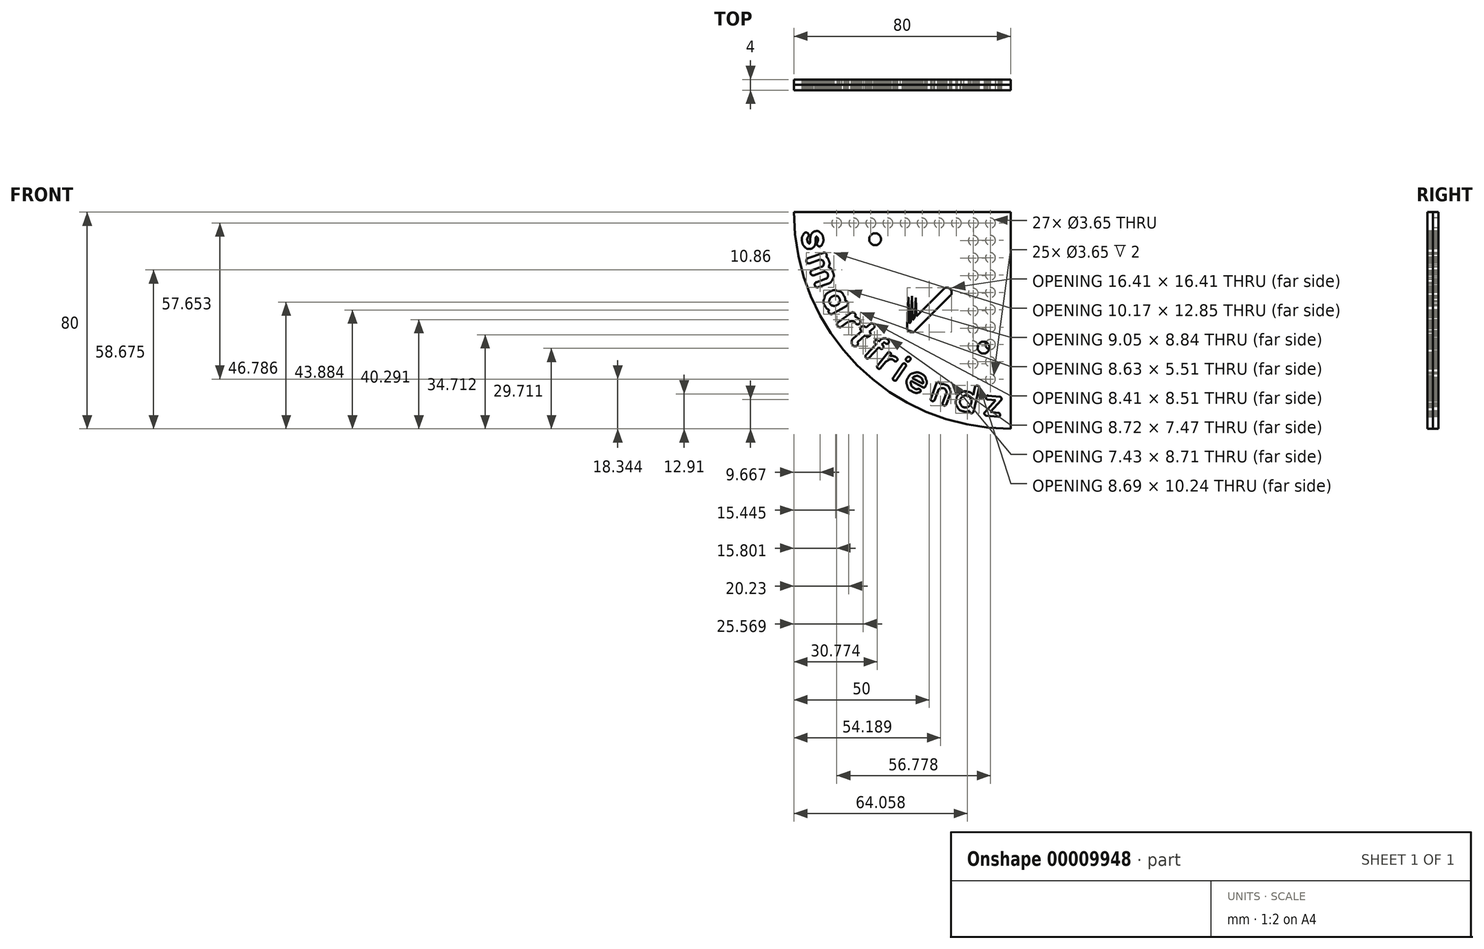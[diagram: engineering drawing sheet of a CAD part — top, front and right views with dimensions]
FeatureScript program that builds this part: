
annotation { "Feature Type Name" : "Feature", "Feature Type Description" : "" }
export const myFeature = defineFeature(function(context is Context, id is Id, definition is map)
    precondition{}
    {
        {
            var Q0;
            Q0=qCreatedBy(makeId("Front.planeOp"),FACE);
            var sketch = newSketch(context, id + "F0", { "sketchPlane" : qUnion([Q0])});
            skFitSpline(sketch, "E0", {"points": [v(17.73, 12.09) * mm, v(17.4, 12.41) * mm, v(16.98, 12.59) * mm, v(16.53, 12.59) * mm]});
            skFitSpline(sketch, "E1", {"points": [v(16.53, 12.59) * mm, v(16.05, 12.59) * mm, v(15.65, 12.41) * mm, v(15.33, 12.09) * mm]});
            skLineSegment(sketch, "E2", {"start": v(15.33, 12.09) * mm, "end": v(5.27, 2.03) * mm});
            skLineSegment(sketch, "E3", {"start": v(5.27, 2.03) * mm, "end": v(5.07, 8.86) * mm});
            skFitSpline(sketch, "E4", {"points": [v(5.07, 8.86) * mm, v(5.04, 8.88) * mm, v(5.02, 8.9) * mm, v(5, 8.93) * mm]});
            skLineSegment(sketch, "E5", {"start": v(5, 8.93) * mm, "end": v(4.72, 1.5) * mm});
            skLineSegment(sketch, "E6", {"start": v(4.72, 1.5) * mm, "end": v(3.94, 0.73) * mm});
            skLineSegment(sketch, "E7", {"start": v(3.94, 0.73) * mm, "end": v(3.67, 9.53) * mm});
            skLineSegment(sketch, "E8", {"start": v(3.67, 9.53) * mm, "end": v(3.64, 9.53) * mm});
            skLineSegment(sketch, "E9", {"start": v(3.64, 9.53) * mm, "end": v(3.32, 0.1) * mm});
            skLineSegment(sketch, "E10", {"start": v(3.32, 0.1) * mm, "end": v(2.64, -0.57) * mm});
            skLineSegment(sketch, "E11", {"start": v(2.64, -0.57) * mm, "end": v(2.37, 9) * mm});
            skFitSpline(sketch, "E12", {"points": [v(2.37, 9) * mm, v(2.35, 9) * mm, v(2.33, 8.97) * mm, v(2.32, 8.93) * mm]});
            skLineSegment(sketch, "E13", {"start": v(2.32, 8.93) * mm, "end": v(1.94, -1.57) * mm});
            skFitSpline(sketch, "E14", {"points": [v(1.94, -1.57) * mm, v(1.9, -1.72) * mm, v(1.87, -1.9) * mm, v(1.87, -2.07) * mm]});
            skFitSpline(sketch, "E15", {"points": [v(1.87, -2.07) * mm, v(1.87, -2.55) * mm, v(2.04, -2.95) * mm, v(2.37, -3.28) * mm]});
            skFitSpline(sketch, "E16", {"points": [v(2.37, -3.28) * mm, v(2.7, -3.6) * mm, v(3.12, -3.78) * mm, v(3.6, -3.8) * mm]});
            skFitSpline(sketch, "E17", {"points": [v(3.6, -3.8) * mm, v(4.07, -3.8) * mm, v(4.47, -3.65) * mm, v(4.82, -3.3) * mm]});
            skLineSegment(sketch, "E18", {"start": v(4.82, -3.3) * mm, "end": v(17.75, 9.63) * mm});
            skFitSpline(sketch, "E19", {"points": [v(17.75, 9.63) * mm, v(18.08, 9.98) * mm, v(18.25, 10.38) * mm, v(18.25, 10.86) * mm]});
            skFitSpline(sketch, "E20", {"points": [v(18.25, 10.86) * mm, v(18.23, 11.34) * mm, v(18.08, 11.76) * mm, v(17.73, 12.09) * mm]});
            skFitSpline(sketch, "E21", {"points": [v(9.35, 19.77) * mm, v(9.35, 20.24) * mm, v(9.17, 20.64) * mm, v(8.82, 21) * mm]});
            skFitSpline(sketch, "E22", {"points": [v(8.82, 21) * mm, v(8.5, 21.32) * mm, v(8.07, 21.5) * mm, v(7.62, 21.5) * mm]});
            skFitSpline(sketch, "E23", {"points": [v(7.62, 21.5) * mm, v(7.45, 21.5) * mm, v(7.3, 21.47) * mm, v(7.15, 21.42) * mm]});
            skLineSegment(sketch, "E24", {"start": v(7.15, 21.42) * mm, "end": v(-3.41, 21.1) * mm});
            skFitSpline(sketch, "E25", {"points": [v(-3.41, 21.1) * mm, v(-3.44, 21.07) * mm, v(-3.46, 21.07) * mm, v(-3.46, 21.04) * mm]});
            skLineSegment(sketch, "E26", {"start": v(-3.46, 21.04) * mm, "end": v(6.15, 20.7) * mm});
            skLineSegment(sketch, "E27", {"start": v(6.15, 20.7) * mm, "end": v(5.47, 20.02) * mm});
            skLineSegment(sketch, "E28", {"start": v(5.47, 20.02) * mm, "end": v(-4.09, 19.74) * mm});
            skLineSegment(sketch, "E29", {"start": v(-4.09, 19.74) * mm, "end": v(4.84, 19.42) * mm});
            skLineSegment(sketch, "E30", {"start": v(4.84, 19.42) * mm, "end": v(4.07, 18.64) * mm});
            skLineSegment(sketch, "E31", {"start": v(4.07, 18.64) * mm, "end": v(-3.56, 18.42) * mm});
            skFitSpline(sketch, "E32", {"points": [v(-3.56, 18.42) * mm, v(-3.54, 18.4) * mm, v(-3.54, 18.4) * mm, v(-3.51, 18.37) * mm]});
            skLineSegment(sketch, "E33", {"start": v(-3.51, 18.37) * mm, "end": v(3.57, 18.11) * mm});
            skLineSegment(sketch, "E34", {"start": v(3.57, 18.11) * mm, "end": v(-6.54, 8.06) * mm});
            skFitSpline(sketch, "E35", {"points": [v(-6.54, 8.06) * mm, v(-6.86, 7.73) * mm, v(-7.04, 7.3) * mm, v(-7.04, 6.86) * mm]});
            skFitSpline(sketch, "E36", {"points": [v(-7.04, 6.86) * mm, v(-7.04, 6.38) * mm, v(-6.86, 5.98) * mm, v(-6.54, 5.66) * mm]});
            skFitSpline(sketch, "E37", {"points": [v(-6.54, 5.66) * mm, v(-6.21, 5.33) * mm, v(-5.79, 5.16) * mm, v(-5.31, 5.13) * mm]});
            skFitSpline(sketch, "E38", {"points": [v(-5.31, 5.13) * mm, v(-4.84, 5.13) * mm, v(-4.44, 5.28) * mm, v(-4.09, 5.63) * mm]});
            skLineSegment(sketch, "E39", {"start": v(-4.09, 5.63) * mm, "end": v(8.85, 18.57) * mm});
            skFitSpline(sketch, "E40", {"points": [v(8.85, 18.57) * mm, v(9.2, 18.9) * mm, v(9.35, 19.3) * mm, v(9.35, 19.77) * mm]});
            skFitSpline(sketch, "E41", {"points": [v(-33.8, 26.97) * mm, v(-33.43, 27.05) * mm, v(-33.08, 27.22) * mm, v(-32.76, 27.52) * mm]});
            skFitSpline(sketch, "E42", {"points": [v(-32.76, 27.52) * mm, v(-32.43, 27.82) * mm, v(-32.18, 28.22) * mm, v(-32.06, 28.72) * mm]});
            skFitSpline(sketch, "E43", {"points": [v(-32.06, 28.72) * mm, v(-31.93, 29.2) * mm, v(-31.88, 29.7) * mm, v(-31.88, 30.25) * mm]});
            skLineSegment(sketch, "E44", {"start": v(-31.88, 30.25) * mm, "end": v(-31.88, 30.27) * mm});
            skLineSegment(sketch, "E45", {"start": v(-31.88, 30.27) * mm, "end": v(-31.88, 30.32) * mm});
            skFitSpline(sketch, "E46", {"points": [v(-31.88, 30.32) * mm, v(-31.88, 30.82) * mm, v(-31.83, 31.17) * mm, v(-31.73, 31.4) * mm]});
            skFitSpline(sketch, "E47", {"points": [v(-31.73, 31.4) * mm, v(-31.72, 31.45) * mm, v(-31.7, 31.48) * mm, v(-31.68, 31.5) * mm]});
            skFitSpline(sketch, "E48", {"points": [v(-31.68, 31.5) * mm, v(-31.66, 31.52) * mm, v(-31.64, 31.52) * mm, v(-31.6, 31.52) * mm]});
            skFitSpline(sketch, "E49", {"points": [v(-31.6, 31.52) * mm, v(-31.57, 31.52) * mm, v(-31.51, 31.47) * mm, v(-31.43, 31.37) * mm]});
            skFitSpline(sketch, "E50", {"points": [v(-31.43, 31.37) * mm, v(-31.26, 31.2) * mm, v(-31.13, 30.97) * mm, v(-31.06, 30.65) * mm]});
            skFitSpline(sketch, "E51", {"points": [v(-31.06, 30.65) * mm, v(-31, 30.32) * mm, v(-31.08, 29.87) * mm, v(-31.33, 29.3) * mm]});
            skFitSpline(sketch, "E52", {"points": [v(-31.33, 29.3) * mm, v(-31.46, 29.05) * mm, v(-31.46, 28.77) * mm, v(-31.36, 28.52) * mm]});
            skFitSpline(sketch, "E53", {"points": [v(-31.36, 28.52) * mm, v(-31.26, 28.27) * mm, v(-31.08, 28.1) * mm, v(-30.83, 27.97) * mm]});
            skFitSpline(sketch, "E54", {"points": [v(-30.83, 27.97) * mm, v(-30.58, 27.87) * mm, v(-30.33, 27.9) * mm, v(-30.08, 28) * mm]});
            skFitSpline(sketch, "E55", {"points": [v(-30.08, 28) * mm, v(-29.83, 28.1) * mm, v(-29.66, 28.27) * mm, v(-29.56, 28.52) * mm]});
            skFitSpline(sketch, "E56", {"points": [v(-29.56, 28.52) * mm, v(-29.15, 29.45) * mm, v(-29, 30.27) * mm, v(-29.13, 31) * mm]});
            skFitSpline(sketch, "E57", {"points": [v(-29.13, 31) * mm, v(-29.25, 31.72) * mm, v(-29.58, 32.33) * mm, v(-30.08, 32.83) * mm]});
            skFitSpline(sketch, "E58", {"points": [v(-30.08, 32.83) * mm, v(-30.68, 33.35) * mm, v(-31.33, 33.58) * mm, v(-32.03, 33.45) * mm]});
            skFitSpline(sketch, "E59", {"points": [v(-32.03, 33.45) * mm, v(-32.4, 33.38) * mm, v(-32.73, 33.23) * mm, v(-33, 32.98) * mm]});
            skFitSpline(sketch, "E60", {"points": [v(-33, 32.98) * mm, v(-33.33, 32.65) * mm, v(-33.58, 32.25) * mm, v(-33.7, 31.8) * mm]});
            skFitSpline(sketch, "E61", {"points": [v(-33.7, 31.8) * mm, v(-33.83, 31.35) * mm, v(-33.88, 30.85) * mm, v(-33.88, 30.3) * mm]});
            skLineSegment(sketch, "E62", {"start": v(-33.88, 30.3) * mm, "end": v(-33.88, 30.27) * mm});
            skFitSpline(sketch, "E63", {"points": [v(-33.88, 30.27) * mm, v(-33.88, 29.75) * mm, v(-33.96, 29.35) * mm, v(-34.06, 29.1) * mm]});
            skFitSpline(sketch, "E64", {"points": [v(-34.06, 29.1) * mm, v(-34.1, 29.03) * mm, v(-34.12, 28.99) * mm, v(-34.13, 28.97) * mm]});
            skLineSegment(sketch, "E65", {"start": v(-34.13, 28.97) * mm, "end": v(-34.16, 28.95) * mm});
            skFitSpline(sketch, "E66", {"points": [v(-34.16, 28.95) * mm, v(-34.18, 28.93) * mm, v(-34.2, 28.92) * mm, v(-34.26, 28.92) * mm]});
            skFitSpline(sketch, "E67", {"points": [v(-34.26, 28.92) * mm, v(-34.3, 28.92) * mm, v(-34.4, 28.97) * mm, v(-34.5, 29.07) * mm]});
            skFitSpline(sketch, "E68", {"points": [v(-34.5, 29.07) * mm, v(-34.73, 29.3) * mm, v(-34.86, 29.6) * mm, v(-34.93, 29.92) * mm]});
            skFitSpline(sketch, "E69", {"points": [v(-34.93, 29.92) * mm, v(-35.03, 30.42) * mm, v(-34.93, 30.97) * mm, v(-34.6, 31.52) * mm]});
            skFitSpline(sketch, "E70", {"points": [v(-34.6, 31.52) * mm, v(-34.48, 31.75) * mm, v(-34.43, 32) * mm, v(-34.5, 32.28) * mm]});
            skFitSpline(sketch, "E71", {"points": [v(-34.5, 32.28) * mm, v(-34.58, 32.55) * mm, v(-34.76, 32.75) * mm, v(-34.98, 32.85) * mm]});
            skFitSpline(sketch, "E72", {"points": [v(-34.98, 32.85) * mm, v(-35.2, 32.98) * mm, v(-35.46, 33.03) * mm, v(-35.73, 32.93) * mm]});
            skFitSpline(sketch, "E73", {"points": [v(-35.73, 32.93) * mm, v(-36, 32.85) * mm, v(-36.18, 32.7) * mm, v(-36.3, 32.48) * mm]});
            skFitSpline(sketch, "E74", {"points": [v(-36.3, 32.48) * mm, v(-36.84, 31.47) * mm, v(-37.04, 30.5) * mm, v(-36.86, 29.55) * mm]});
            skFitSpline(sketch, "E75", {"points": [v(-36.86, 29.55) * mm, v(-36.71, 28.8) * mm, v(-36.39, 28.17) * mm, v(-35.86, 27.65) * mm]});
            skFitSpline(sketch, "E76", {"points": [v(-35.86, 27.65) * mm, v(-35.36, 27.17) * mm, v(-34.83, 26.95) * mm, v(-34.23, 26.95) * mm]});
            skFitSpline(sketch, "E77", {"points": [v(-34.23, 26.95) * mm, v(-34.08, 26.92) * mm, v(-33.93, 26.95) * mm, v(-33.8, 26.97) * mm]});
            skFitSpline(sketch, "E78", {"points": [v(-25.65, 15.74) * mm, v(-25.25, 16.56) * mm, v(-25.23, 17.44) * mm, v(-25.55, 18.37) * mm]});
            skFitSpline(sketch, "E79", {"points": [v(-25.55, 18.37) * mm, v(-25.85, 19.22) * mm, v(-26.4, 19.82) * mm, v(-27.2, 20.2) * mm]});
            skFitSpline(sketch, "E80", {"points": [v(-27.2, 20.2) * mm, v(-26.83, 21) * mm, v(-26.78, 21.84) * mm, v(-27.1, 22.72) * mm]});
            skFitSpline(sketch, "E81", {"points": [v(-27.1, 22.72) * mm, v(-27.28, 23.22) * mm, v(-27.58, 23.67) * mm, v(-27.98, 24.04) * mm]});
            skFitSpline(sketch, "E82", {"points": [v(-27.98, 24.04) * mm, v(-27.8, 24.3) * mm, v(-27.78, 24.6) * mm, v(-27.88, 24.92) * mm]});
            skFitSpline(sketch, "E83", {"points": [v(-27.88, 24.92) * mm, v(-27.98, 25.17) * mm, v(-28.13, 25.37) * mm, v(-28.38, 25.47) * mm]});
            skFitSpline(sketch, "E84", {"points": [v(-28.38, 25.47) * mm, v(-28.63, 25.6) * mm, v(-28.88, 25.6) * mm, v(-29.15, 25.5) * mm]});
            skLineSegment(sketch, "E85", {"start": v(-29.15, 25.5) * mm, "end": v(-34.7, 23.52) * mm});
            skFitSpline(sketch, "E86", {"points": [v(-34.7, 23.52) * mm, v(-34.93, 23.44) * mm, v(-35.1, 23.3) * mm, v(-35.2, 23.1) * mm]});
            skFitSpline(sketch, "E87", {"points": [v(-35.2, 23.1) * mm, v(-35.3, 22.9) * mm, v(-35.36, 22.7) * mm, v(-35.33, 22.44) * mm]});
            skLineSegment(sketch, "E88", {"start": v(-35.33, 22.44) * mm, "end": v(-35.28, 22.27) * mm});
            skLineSegment(sketch, "E89", {"start": v(-35.28, 22.27) * mm, "end": v(-35.28, 22.24) * mm});
            skFitSpline(sketch, "E90", {"points": [v(-35.28, 22.24) * mm, v(-35.16, 21.87) * mm, v(-34.86, 21.62) * mm, v(-34.43, 21.57) * mm]});
            skLineSegment(sketch, "E91", {"start": v(-34.43, 21.57) * mm, "end": v(-34.38, 21.57) * mm});
            skLineSegment(sketch, "E92", {"start": v(-34.38, 21.57) * mm, "end": v(-34.3, 21.6) * mm});
            skLineSegment(sketch, "E93", {"start": v(-34.3, 21.6) * mm, "end": v(-34.2, 21.6) * mm});
            skLineSegment(sketch, "E94", {"start": v(-34.2, 21.6) * mm, "end": v(-34.06, 21.64) * mm});
            skLineSegment(sketch, "E95", {"start": v(-34.06, 21.64) * mm, "end": v(-30.68, 22.84) * mm});
            skFitSpline(sketch, "E96", {"points": [v(-30.68, 22.84) * mm, v(-30.33, 22.97) * mm, v(-29.98, 22.94) * mm, v(-29.63, 22.8) * mm]});
            skFitSpline(sketch, "E97", {"points": [v(-29.63, 22.8) * mm, v(-29.28, 22.64) * mm, v(-29.05, 22.4) * mm, v(-28.95, 22.04) * mm]});
            skFitSpline(sketch, "E98", {"points": [v(-28.95, 22.04) * mm, v(-28.83, 21.7) * mm, v(-28.85, 21.37) * mm, v(-29, 21.02) * mm]});
            skFitSpline(sketch, "E99", {"points": [v(-29, 21.02) * mm, v(-29.15, 20.67) * mm, v(-29.4, 20.44) * mm, v(-29.73, 20.32) * mm]});
            skLineSegment(sketch, "E100", {"start": v(-29.73, 20.32) * mm, "end": v(-33.13, 19.12) * mm});
            skFitSpline(sketch, "E101", {"points": [v(-33.13, 19.12) * mm, v(-33.38, 19.04) * mm, v(-33.56, 18.87) * mm, v(-33.68, 18.6) * mm]});
            skFitSpline(sketch, "E102", {"points": [v(-33.68, 18.6) * mm, v(-33.8, 18.34) * mm, v(-33.8, 18.09) * mm, v(-33.73, 17.84) * mm]});
            skFitSpline(sketch, "E103", {"points": [v(-33.73, 17.84) * mm, v(-33.63, 17.59) * mm, v(-33.48, 17.41) * mm, v(-33.23, 17.29) * mm]});
            skFitSpline(sketch, "E104", {"points": [v(-33.23, 17.29) * mm, v(-32.98, 17.16) * mm, v(-32.73, 17.16) * mm, v(-32.48, 17.24) * mm]});
            skLineSegment(sketch, "E105", {"start": v(-32.48, 17.24) * mm, "end": v(-29.1, 18.44) * mm});
            skFitSpline(sketch, "E106", {"points": [v(-29.1, 18.44) * mm, v(-28.75, 18.54) * mm, v(-28.4, 18.52) * mm, v(-28.08, 18.37) * mm]});
            skFitSpline(sketch, "E107", {"points": [v(-28.08, 18.37) * mm, v(-27.75, 18.2) * mm, v(-27.53, 17.94) * mm, v(-27.4, 17.61) * mm]});
            skFitSpline(sketch, "E108", {"points": [v(-27.4, 17.61) * mm, v(-27.28, 17.26) * mm, v(-27.3, 16.94) * mm, v(-27.45, 16.59) * mm]});
            skFitSpline(sketch, "E109", {"points": [v(-27.45, 16.59) * mm, v(-27.6, 16.24) * mm, v(-27.88, 16.01) * mm, v(-28.23, 15.89) * mm]});
            skLineSegment(sketch, "E110", {"start": v(-28.23, 15.89) * mm, "end": v(-31.58, 14.69) * mm});
            skFitSpline(sketch, "E111", {"points": [v(-31.58, 14.69) * mm, v(-31.83, 14.59) * mm, v(-32.03, 14.41) * mm, v(-32.13, 14.16) * mm]});
            skFitSpline(sketch, "E112", {"points": [v(-32.13, 14.16) * mm, v(-32.26, 13.91) * mm, v(-32.26, 13.66) * mm, v(-32.16, 13.41) * mm]});
            skFitSpline(sketch, "E113", {"points": [v(-32.16, 13.41) * mm, v(-32.06, 13.16) * mm, v(-31.9, 12.96) * mm, v(-31.66, 12.86) * mm]});
            skFitSpline(sketch, "E114", {"points": [v(-31.66, 12.86) * mm, v(-31.53, 12.79) * mm, v(-31.38, 12.76) * mm, v(-31.23, 12.76) * mm]});
            skFitSpline(sketch, "E115", {"points": [v(-31.23, 12.76) * mm, v(-31.13, 12.76) * mm, v(-31, 12.79) * mm, v(-30.9, 12.81) * mm]});
            skLineSegment(sketch, "E116", {"start": v(-30.9, 12.81) * mm, "end": v(-27.55, 14.01) * mm});
            skFitSpline(sketch, "E117", {"points": [v(-27.55, 14.01) * mm, v(-26.68, 14.34) * mm, v(-26.05, 14.91) * mm, v(-25.65, 15.74) * mm]});
            skFitSpline(sketch, "E118", {"points": [v(-20.05, 6.53) * mm, v(-19.97, 6.8) * mm, v(-20, 7.03) * mm, v(-20.12, 7.26) * mm]});
            skFitSpline(sketch, "E119", {"points": [v(-20.12, 7.26) * mm, v(-20.25, 7.48) * mm, v(-20.42, 7.63) * mm, v(-20.65, 7.7) * mm]});
            skFitSpline(sketch, "E120", {"points": [v(-20.65, 7.7) * mm, v(-20.77, 7.76) * mm, v(-20.92, 7.78) * mm, v(-21.05, 7.76) * mm]});
            skFitSpline(sketch, "E121", {"points": [v(-21.05, 7.76) * mm, v(-21.02, 8.46) * mm, v(-21.15, 9.1) * mm, v(-21.5, 9.68) * mm]});
            skFitSpline(sketch, "E122", {"points": [v(-21.5, 9.68) * mm, v(-22.02, 10.6) * mm, v(-22.8, 11.21) * mm, v(-23.83, 11.46) * mm]});
            skFitSpline(sketch, "E123", {"points": [v(-23.83, 11.46) * mm, v(-24.85, 11.71) * mm, v(-25.85, 11.56) * mm, v(-26.78, 11.03) * mm]});
            skFitSpline(sketch, "E124", {"points": [v(-26.78, 11.03) * mm, v(-27.73, 10.5) * mm, v(-28.35, 9.73) * mm, v(-28.68, 8.73) * mm]});
            skFitSpline(sketch, "E125", {"points": [v(-28.68, 8.73) * mm, v(-29, 7.73) * mm, v(-28.9, 6.76) * mm, v(-28.38, 5.83) * mm]});
            skFitSpline(sketch, "E126", {"points": [v(-28.38, 5.83) * mm, v(-28.05, 5.23) * mm, v(-27.58, 4.78) * mm, v(-26.98, 4.43) * mm]});
            skFitSpline(sketch, "E127", {"points": [v(-26.98, 4.43) * mm, v(-27.05, 4.3) * mm, v(-27.1, 4.18) * mm, v(-27.13, 4.05) * mm]});
            skFitSpline(sketch, "E128", {"points": [v(-27.13, 4.05) * mm, v(-27.18, 3.83) * mm, v(-27.13, 3.6) * mm, v(-27, 3.38) * mm]});
            skFitSpline(sketch, "E129", {"points": [v(-27, 3.38) * mm, v(-26.88, 3.15) * mm, v(-26.68, 3) * mm, v(-26.43, 2.93) * mm]});
            skFitSpline(sketch, "E130", {"points": [v(-26.43, 2.93) * mm, v(-26.33, 2.9) * mm, v(-26.25, 2.88) * mm, v(-26.15, 2.88) * mm]});
            skFitSpline(sketch, "E131", {"points": [v(-26.15, 2.88) * mm, v(-26, 2.88) * mm, v(-25.83, 2.93) * mm, v(-25.68, 3) * mm]});
            skLineSegment(sketch, "E132", {"start": v(-25.68, 3) * mm, "end": v(-20.52, 5.88) * mm});
            skFitSpline(sketch, "E133", {"points": [v(-20.52, 5.88) * mm, v(-20.27, 6.08) * mm, v(-20.12, 6.28) * mm, v(-20.05, 6.53) * mm]});
            skFitSpline(sketch, "E134", {"points": [v(-23.1, 7.36) * mm, v(-23.28, 6.86) * mm, v(-23.58, 6.48) * mm, v(-24.08, 6.2) * mm]});
            skFitSpline(sketch, "E135", {"points": [v(-24.08, 6.2) * mm, v(-24.55, 5.93) * mm, v(-25.05, 5.86) * mm, v(-25.53, 5.98) * mm]});
            skFitSpline(sketch, "E136", {"points": [v(-25.53, 5.98) * mm, v(-26.03, 6.1) * mm, v(-26.38, 6.38) * mm, v(-26.63, 6.83) * mm]});
            skFitSpline(sketch, "E137", {"points": [v(-26.63, 6.83) * mm, v(-26.88, 7.28) * mm, v(-26.93, 7.73) * mm, v(-26.75, 8.2) * mm]});
            skFitSpline(sketch, "E138", {"points": [v(-26.75, 8.2) * mm, v(-26.58, 8.68) * mm, v(-26.28, 9.06) * mm, v(-25.78, 9.33) * mm]});
            skFitSpline(sketch, "E139", {"points": [v(-25.78, 9.33) * mm, v(-25.43, 9.53) * mm, v(-25.08, 9.63) * mm, v(-24.73, 9.63) * mm]});
            skFitSpline(sketch, "E140", {"points": [v(-24.73, 9.63) * mm, v(-24.58, 9.63) * mm, v(-24.43, 9.6) * mm, v(-24.3, 9.58) * mm]});
            skFitSpline(sketch, "E141", {"points": [v(-24.3, 9.58) * mm, v(-23.8, 9.48) * mm, v(-23.45, 9.2) * mm, v(-23.2, 8.76) * mm]});
            skFitSpline(sketch, "E142", {"points": [v(-23.2, 8.76) * mm, v(-22.98, 8.3) * mm, v(-22.93, 7.86) * mm, v(-23.1, 7.36) * mm]});
            skFitSpline(sketch, "E143", {"points": [v(-17.2, -0.47) * mm, v(-17.05, -0.7) * mm, v(-16.82, -0.82) * mm, v(-16.55, -0.87) * mm]});
            skFitSpline(sketch, "E144", {"points": [v(-16.55, -0.87) * mm, v(-16.27, -0.92) * mm, v(-16.02, -0.85) * mm, v(-15.82, -0.7) * mm]});
            skFitSpline(sketch, "E145", {"points": [v(-15.82, -0.7) * mm, v(-15.6, -0.55) * mm, v(-15.47, -0.32) * mm, v(-15.45, -0.07) * mm]});
            skFitSpline(sketch, "E146", {"points": [v(-15.45, -0.07) * mm, v(-15.4, 0.18) * mm, v(-15.5, 0.48) * mm, v(-15.72, 0.78) * mm]});
            skFitSpline(sketch, "E147", {"points": [v(-15.72, 0.78) * mm, v(-15.92, 1.08) * mm, v(-16.22, 1.33) * mm, v(-16.62, 1.58) * mm]});
            skFitSpline(sketch, "E148", {"points": [v(-16.62, 1.58) * mm, v(-16.87, 1.73) * mm, v(-17.15, 1.85) * mm, v(-17.4, 1.93) * mm]});
            skFitSpline(sketch, "E149", {"points": [v(-17.4, 1.93) * mm, v(-17.3, 2.05) * mm, v(-17.25, 2.2) * mm, v(-17.22, 2.38) * mm]});
            skFitSpline(sketch, "E150", {"points": [v(-17.22, 2.38) * mm, v(-17.2, 2.65) * mm, v(-17.25, 2.88) * mm, v(-17.42, 3.1) * mm]});
            skFitSpline(sketch, "E151", {"points": [v(-17.42, 3.1) * mm, v(-17.57, 3.33) * mm, v(-17.8, 3.45) * mm, v(-18.05, 3.5) * mm]});
            skFitSpline(sketch, "E152", {"points": [v(-18.05, 3.5) * mm, v(-18.32, 3.55) * mm, v(-18.55, 3.5) * mm, v(-18.77, 3.33) * mm]});
            skLineSegment(sketch, "E153", {"start": v(-18.77, 3.33) * mm, "end": v(-23.58, -0.12) * mm});
            skFitSpline(sketch, "E154", {"points": [v(-23.58, -0.12) * mm, v(-23.8, -0.27) * mm, v(-23.93, -0.5) * mm, v(-23.98, -0.77) * mm]});
            skFitSpline(sketch, "E155", {"points": [v(-23.98, -0.77) * mm, v(-24.03, -1.05) * mm, v(-23.95, -1.3) * mm, v(-23.8, -1.52) * mm]});
            skFitSpline(sketch, "E156", {"points": [v(-23.8, -1.52) * mm, v(-23.65, -1.75) * mm, v(-23.43, -1.87) * mm, v(-23.15, -1.92) * mm]});
            skFitSpline(sketch, "E157", {"points": [v(-23.15, -1.92) * mm, v(-23.1, -1.92) * mm, v(-23.03, -1.95) * mm, v(-22.98, -1.95) * mm]});
            skFitSpline(sketch, "E158", {"points": [v(-22.98, -1.95) * mm, v(-22.78, -1.95) * mm, v(-22.6, -1.9) * mm, v(-22.43, -1.77) * mm]});
            skLineSegment(sketch, "E159", {"start": v(-22.43, -1.77) * mm, "end": v(-20.15, -0.12) * mm});
            skFitSpline(sketch, "E160", {"points": [v(-20.15, -0.12) * mm, v(-18.67, 0.33) * mm, v(-17.7, 0.2) * mm, v(-17.2, -0.47) * mm]});
            skFitSpline(sketch, "E161", {"points": [v(-10.2, -1.62) * mm, v(-10.17, -1.35) * mm, v(-10.27, -1.1) * mm, v(-10.44, -0.9) * mm]});
            skFitSpline(sketch, "E162", {"points": [v(-10.44, -0.9) * mm, v(-10.62, -0.7) * mm, v(-10.87, -0.57) * mm, v(-11.14, -0.55) * mm]});
            skFitSpline(sketch, "E163", {"points": [v(-11.14, -0.55) * mm, v(-11.42, -0.52) * mm, v(-11.67, -0.6) * mm, v(-11.9, -0.8) * mm]});
            skLineSegment(sketch, "E164", {"start": v(-11.9, -0.8) * mm, "end": v(-13.4, -2.1) * mm});
            skLineSegment(sketch, "E165", {"start": v(-13.4, -2.1) * mm, "end": v(-13.57, -1.92) * mm});
            skFitSpline(sketch, "E166", {"points": [v(-13.57, -1.92) * mm, v(-13.74, -1.72) * mm, v(-14, -1.6) * mm, v(-14.27, -1.57) * mm]});
            skFitSpline(sketch, "E167", {"points": [v(-14.27, -1.57) * mm, v(-14.54, -1.55) * mm, v(-14.8, -1.65) * mm, v(-15, -1.82) * mm]});
            skFitSpline(sketch, "E168", {"points": [v(-15, -1.82) * mm, v(-15.2, -2) * mm, v(-15.32, -2.25) * mm, v(-15.35, -2.52) * mm]});
            skFitSpline(sketch, "E169", {"points": [v(-15.35, -2.52) * mm, v(-15.37, -2.8) * mm, v(-15.27, -3.05) * mm, v(-15.1, -3.25) * mm]});
            skLineSegment(sketch, "E170", {"start": v(-15.1, -3.25) * mm, "end": v(-14.92, -3.43) * mm});
            skLineSegment(sketch, "E171", {"start": v(-14.92, -3.43) * mm, "end": v(-17.92, -6.05) * mm});
            skFitSpline(sketch, "E172", {"points": [v(-17.92, -6.05) * mm, v(-18.3, -6.38) * mm, v(-18.52, -6.83) * mm, v(-18.55, -7.33) * mm]});
            skFitSpline(sketch, "E173", {"points": [v(-18.55, -7.33) * mm, v(-18.57, -7.83) * mm, v(-18.42, -8.28) * mm, v(-18.1, -8.68) * mm]});
            skFitSpline(sketch, "E174", {"points": [v(-18.1, -8.68) * mm, v(-17.92, -8.88) * mm, v(-17.67, -9) * mm, v(-17.4, -9.03) * mm]});
            skFitSpline(sketch, "E175", {"points": [v(-17.4, -9.03) * mm, v(-17.37, -9.03) * mm, v(-17.35, -9.03) * mm, v(-17.32, -9.03) * mm]});
            skFitSpline(sketch, "E176", {"points": [v(-17.32, -9.03) * mm, v(-17.07, -9.03) * mm, v(-16.85, -8.95) * mm, v(-16.67, -8.78) * mm]});
            skFitSpline(sketch, "E177", {"points": [v(-16.67, -8.78) * mm, v(-16.47, -8.6) * mm, v(-16.35, -8.35) * mm, v(-16.32, -8.08) * mm]});
            skFitSpline(sketch, "E178", {"points": [v(-16.32, -8.08) * mm, v(-16.3, -7.85) * mm, v(-16.35, -7.65) * mm, v(-16.45, -7.48) * mm]});
            skLineSegment(sketch, "E179", {"start": v(-16.45, -7.48) * mm, "end": v(-13.57, -4.95) * mm});
            skLineSegment(sketch, "E180", {"start": v(-13.57, -4.95) * mm, "end": v(-13.44, -5.1) * mm});
            skFitSpline(sketch, "E181", {"points": [v(-13.44, -5.1) * mm, v(-13.27, -5.3) * mm, v(-13.02, -5.43) * mm, v(-12.74, -5.45) * mm]});
            skFitSpline(sketch, "E182", {"points": [v(-12.74, -5.45) * mm, v(-12.47, -5.48) * mm, v(-12.22, -5.38) * mm, v(-12, -5.2) * mm]});
            skFitSpline(sketch, "E183", {"points": [v(-12, -5.2) * mm, v(-11.8, -5.03) * mm, v(-11.67, -4.78) * mm, v(-11.67, -4.5) * mm]});
            skFitSpline(sketch, "E184", {"points": [v(-11.67, -4.5) * mm, v(-11.64, -4.23) * mm, v(-11.74, -3.98) * mm, v(-11.92, -3.78) * mm]});
            skLineSegment(sketch, "E185", {"start": v(-11.92, -3.78) * mm, "end": v(-12.04, -3.63) * mm});
            skLineSegment(sketch, "E186", {"start": v(-12.04, -3.63) * mm, "end": v(-10.54, -2.32) * mm});
            skFitSpline(sketch, "E187", {"points": [v(-10.54, -2.32) * mm, v(-10.32, -2.15) * mm, v(-10.2, -1.9) * mm, v(-10.2, -1.62) * mm]});
            skFitSpline(sketch, "E188", {"points": [v(-4.81, -7.33) * mm, v(-4.81, -7.1) * mm, v(-4.89, -6.93) * mm, v(-5.04, -6.8) * mm]});
            skFitSpline(sketch, "E189", {"points": [v(-5.04, -6.8) * mm, v(-5.56, -6.3) * mm, v(-6.11, -6.05) * mm, v(-6.66, -6.1) * mm]});
            skFitSpline(sketch, "E190", {"points": [v(-6.66, -6.1) * mm, v(-7.21, -6.15) * mm, v(-7.76, -6.45) * mm, v(-8.34, -7.05) * mm]});
            skLineSegment(sketch, "E191", {"start": v(-8.34, -7.05) * mm, "end": v(-8.54, -7.25) * mm});
            skLineSegment(sketch, "E192", {"start": v(-8.54, -7.25) * mm, "end": v(-8.87, -6.93) * mm});
            skFitSpline(sketch, "E193", {"points": [v(-8.87, -6.93) * mm, v(-9.02, -6.78) * mm, v(-9.2, -6.7) * mm, v(-9.42, -6.7) * mm]});
            skFitSpline(sketch, "E194", {"points": [v(-9.42, -6.7) * mm, v(-9.64, -6.7) * mm, v(-9.82, -6.78) * mm, v(-9.97, -6.93) * mm]});
            skFitSpline(sketch, "E195", {"points": [v(-9.97, -6.93) * mm, v(-10.12, -7.08) * mm, v(-10.2, -7.25) * mm, v(-10.17, -7.48) * mm]});
            skFitSpline(sketch, "E196", {"points": [v(-10.17, -7.48) * mm, v(-10.17, -7.7) * mm, v(-10.1, -7.88) * mm, v(-9.92, -8.03) * mm]});
            skLineSegment(sketch, "E197", {"start": v(-9.92, -8.03) * mm, "end": v(-9.6, -8.35) * mm});
            skLineSegment(sketch, "E198", {"start": v(-9.6, -8.35) * mm, "end": v(-9.64, -8.4) * mm});
            skLineSegment(sketch, "E199", {"start": v(-9.64, -8.4) * mm, "end": v(-13.3, -12.2) * mm});
            skFitSpline(sketch, "E200", {"points": [v(-13.3, -12.2) * mm, v(-13.44, -12.36) * mm, v(-13.52, -12.53) * mm, v(-13.52, -12.76) * mm]});
            skFitSpline(sketch, "E201", {"points": [v(-13.52, -12.76) * mm, v(-13.52, -12.96) * mm, v(-13.44, -13.13) * mm, v(-13.3, -13.28) * mm]});
            skFitSpline(sketch, "E202", {"points": [v(-13.3, -13.28) * mm, v(-13.14, -13.43) * mm, v(-12.97, -13.5) * mm, v(-12.74, -13.5) * mm]});
            skFitSpline(sketch, "E203", {"points": [v(-12.74, -13.5) * mm, v(-12.54, -13.5) * mm, v(-12.37, -13.43) * mm, v(-12.22, -13.28) * mm]});
            skLineSegment(sketch, "E204", {"start": v(-12.22, -13.28) * mm, "end": v(-8.52, -9.4) * mm});
            skLineSegment(sketch, "E205", {"start": v(-8.52, -9.4) * mm, "end": v(-8.14, -9.75) * mm});
            skFitSpline(sketch, "E206", {"points": [v(-8.14, -9.75) * mm, v(-7.99, -9.9) * mm, v(-7.81, -9.98) * mm, v(-7.59, -9.95) * mm]});
            skFitSpline(sketch, "E207", {"points": [v(-7.59, -9.95) * mm, v(-7.36, -9.95) * mm, v(-7.19, -9.88) * mm, v(-7.06, -9.73) * mm]});
            skFitSpline(sketch, "E208", {"points": [v(-7.06, -9.73) * mm, v(-6.91, -9.58) * mm, v(-6.84, -9.4) * mm, v(-6.86, -9.18) * mm]});
            skFitSpline(sketch, "E209", {"points": [v(-6.86, -9.18) * mm, v(-6.86, -8.98) * mm, v(-6.94, -8.8) * mm, v(-7.09, -8.65) * mm]});
            skLineSegment(sketch, "E210", {"start": v(-7.09, -8.65) * mm, "end": v(-7.46, -8.3) * mm});
            skLineSegment(sketch, "E211", {"start": v(-7.46, -8.3) * mm, "end": v(-7.26, -8.1) * mm});
            skFitSpline(sketch, "E212", {"points": [v(-7.26, -8.1) * mm, v(-7.14, -7.98) * mm, v(-7.01, -7.85) * mm, v(-6.89, -7.75) * mm]});
            skFitSpline(sketch, "E213", {"points": [v(-6.89, -7.75) * mm, v(-6.76, -7.65) * mm, v(-6.66, -7.58) * mm, v(-6.59, -7.63) * mm]});
            skFitSpline(sketch, "E214", {"points": [v(-6.59, -7.63) * mm, v(-6.49, -7.63) * mm, v(-6.36, -7.73) * mm, v(-6.16, -7.9) * mm]});
            skFitSpline(sketch, "E215", {"points": [v(-6.16, -7.9) * mm, v(-5.99, -8.05) * mm, v(-5.81, -8.13) * mm, v(-5.59, -8.13) * mm]});
            skFitSpline(sketch, "E216", {"points": [v(-5.59, -8.13) * mm, v(-5.36, -8.13) * mm, v(-5.19, -8.05) * mm, v(-5.06, -7.9) * mm]});
            skFitSpline(sketch, "E217", {"points": [v(-5.06, -7.9) * mm, v(-4.89, -7.73) * mm, v(-4.81, -7.55) * mm, v(-4.81, -7.33) * mm]});
            skFitSpline(sketch, "E218", {"points": [v(-2.36, -14.56) * mm, v(-2.16, -14.53) * mm, v(-1.99, -14.43) * mm, v(-1.86, -14.28) * mm]});
            skFitSpline(sketch, "E219", {"points": [v(-1.86, -14.28) * mm, v(-1.74, -14.13) * mm, v(-1.69, -13.96) * mm, v(-1.71, -13.76) * mm]});
            skFitSpline(sketch, "E220", {"points": [v(-1.71, -13.76) * mm, v(-1.74, -13.56) * mm, v(-1.86, -13.36) * mm, v(-2.11, -13.16) * mm]});
            skFitSpline(sketch, "E221", {"points": [v(-2.11, -13.16) * mm, v(-2.36, -12.96) * mm, v(-2.69, -12.78) * mm, v(-3.09, -12.68) * mm]});
            skFitSpline(sketch, "E222", {"points": [v(-3.09, -12.68) * mm, v(-3.49, -12.56) * mm, v(-3.86, -12.53) * mm, v(-4.21, -12.6) * mm]});
            skLineSegment(sketch, "E223", {"start": v(-4.21, -12.6) * mm, "end": v(-4.39, -12.63) * mm});
            skLineSegment(sketch, "E224", {"start": v(-4.39, -12.63) * mm, "end": v(-4.21, -12.4) * mm});
            skFitSpline(sketch, "E225", {"points": [v(-4.21, -12.4) * mm, v(-4.09, -12.26) * mm, v(-4.04, -12.08) * mm, v(-4.06, -11.88) * mm]});
            skFitSpline(sketch, "E226", {"points": [v(-4.06, -11.88) * mm, v(-4.09, -11.68) * mm, v(-4.19, -11.5) * mm, v(-4.34, -11.38) * mm]});
            skFitSpline(sketch, "E227", {"points": [v(-4.34, -11.38) * mm, v(-4.49, -11.26) * mm, v(-4.64, -11.2) * mm, v(-4.81, -11.2) * mm]});
            skFitSpline(sketch, "E228", {"points": [v(-4.81, -11.2) * mm, v(-4.83, -11.2) * mm, v(-4.85, -11.2) * mm, v(-4.89, -11.2) * mm]});
            skFitSpline(sketch, "E229", {"points": [v(-4.89, -11.2) * mm, v(-5.09, -11.23) * mm, v(-5.24, -11.3) * mm, v(-5.36, -11.48) * mm]});
            skLineSegment(sketch, "E230", {"start": v(-5.36, -11.48) * mm, "end": v(-9.07, -16.08) * mm});
            skFitSpline(sketch, "E231", {"points": [v(-9.07, -16.08) * mm, v(-9.2, -16.23) * mm, v(-9.24, -16.4) * mm, v(-9.22, -16.63) * mm]});
            skFitSpline(sketch, "E232", {"points": [v(-9.22, -16.63) * mm, v(-9.2, -16.83) * mm, v(-9.1, -17) * mm, v(-8.94, -17.14) * mm]});
            skFitSpline(sketch, "E233", {"points": [v(-8.94, -17.14) * mm, v(-8.77, -17.26) * mm, v(-8.6, -17.31) * mm, v(-8.4, -17.31) * mm]});
            skFitSpline(sketch, "E234", {"points": [v(-8.4, -17.31) * mm, v(-8.19, -17.29) * mm, v(-8.01, -17.21) * mm, v(-7.89, -17.04) * mm]});
            skLineSegment(sketch, "E235", {"start": v(-7.89, -17.04) * mm, "end": v(-6.09, -14.78) * mm});
            skFitSpline(sketch, "E236", {"points": [v(-6.09, -14.78) * mm, v(-4.71, -13.93) * mm, v(-3.61, -13.8) * mm, v(-2.89, -14.4) * mm]});
            skFitSpline(sketch, "E237", {"points": [v(-2.89, -14.4) * mm, v(-2.74, -14.53) * mm, v(-2.56, -14.58) * mm, v(-2.36, -14.56) * mm]});
            skFitSpline(sketch, "E238", {"points": [v(1.12, -15.48) * mm, v(1, -15.38) * mm, v(0.84, -15.36) * mm, v(0.7, -15.36) * mm]});
            skFitSpline(sketch, "E239", {"points": [v(0.7, -15.36) * mm, v(0.64, -15.36) * mm, v(0.6, -15.36) * mm, v(0.54, -15.38) * mm]});
            skFitSpline(sketch, "E240", {"points": [v(0.54, -15.38) * mm, v(0.34, -15.43) * mm, v(0.2, -15.53) * mm, v(0.07, -15.7) * mm]});
            skLineSegment(sketch, "E241", {"start": v(0.07, -15.7) * mm, "end": v(-3.24, -20.54) * mm});
            skFitSpline(sketch, "E242", {"points": [v(-3.24, -20.54) * mm, v(-3.36, -20.71) * mm, v(-3.39, -20.89) * mm, v(-3.36, -21.09) * mm]});
            skFitSpline(sketch, "E243", {"points": [v(-3.36, -21.09) * mm, v(-3.31, -21.29) * mm, v(-3.21, -21.46) * mm, v(-3.04, -21.56) * mm]});
            skFitSpline(sketch, "E244", {"points": [v(-3.04, -21.56) * mm, v(-2.86, -21.69) * mm, v(-2.69, -21.71) * mm, v(-2.49, -21.69) * mm]});
            skFitSpline(sketch, "E245", {"points": [v(-2.49, -21.69) * mm, v(-2.29, -21.64) * mm, v(-2.14, -21.54) * mm, v(-2.01, -21.36) * mm]});
            skLineSegment(sketch, "E246", {"start": v(-2.01, -21.36) * mm, "end": v(1.3, -16.53) * mm});
            skFitSpline(sketch, "E247", {"points": [v(1.3, -16.53) * mm, v(1.42, -16.36) * mm, v(1.47, -16.16) * mm, v(1.42, -15.96) * mm]});
            skFitSpline(sketch, "E248", {"points": [v(1.42, -15.96) * mm, v(1.4, -15.76) * mm, v(1.3, -15.58) * mm, v(1.12, -15.48) * mm]});
            skFitSpline(sketch, "E249", {"points": [v(2.34, -14.6) * mm, v(2.54, -14.56) * mm, v(2.7, -14.46) * mm, v(2.82, -14.28) * mm]});
            skLineSegment(sketch, "E250", {"start": v(2.82, -14.28) * mm, "end": v(3, -14.03) * mm});
            skFitSpline(sketch, "E251", {"points": [v(3, -14.03) * mm, v(3.12, -13.86) * mm, v(3.14, -13.68) * mm, v(3.12, -13.48) * mm]});
            skFitSpline(sketch, "E252", {"points": [v(3.12, -13.48) * mm, v(3.07, -13.28) * mm, v(2.97, -13.13) * mm, v(2.8, -13) * mm]});
            skFitSpline(sketch, "E253", {"points": [v(2.8, -13) * mm, v(2.67, -12.9) * mm, v(2.52, -12.88) * mm, v(2.37, -12.88) * mm]});
            skFitSpline(sketch, "E254", {"points": [v(2.37, -12.88) * mm, v(2.32, -12.88) * mm, v(2.27, -12.88) * mm, v(2.22, -12.9) * mm]});
            skFitSpline(sketch, "E255", {"points": [v(2.22, -12.9) * mm, v(2.02, -12.96) * mm, v(1.84, -13.06) * mm, v(1.74, -13.2) * mm]});
            skLineSegment(sketch, "E256", {"start": v(1.74, -13.2) * mm, "end": v(1.57, -13.46) * mm});
            skFitSpline(sketch, "E257", {"points": [v(1.57, -13.46) * mm, v(1.44, -13.63) * mm, v(1.42, -13.83) * mm, v(1.44, -14.03) * mm]});
            skFitSpline(sketch, "E258", {"points": [v(1.44, -14.03) * mm, v(1.5, -14.23) * mm, v(1.6, -14.4) * mm, v(1.77, -14.5) * mm]});
            skFitSpline(sketch, "E259", {"points": [v(1.77, -14.5) * mm, v(1.97, -14.6) * mm, v(2.14, -14.66) * mm, v(2.34, -14.6) * mm]});
            skFitSpline(sketch, "E260", {"points": [v(7.1, -19.11) * mm, v(6.57, -18.84) * mm, v(6.02, -18.69) * mm, v(5.47, -18.69) * mm]});
            skFitSpline(sketch, "E261", {"points": [v(5.47, -18.69) * mm, v(5.12, -18.69) * mm, v(4.74, -18.74) * mm, v(4.37, -18.86) * mm]});
            skFitSpline(sketch, "E262", {"points": [v(4.37, -18.86) * mm, v(3.42, -19.16) * mm, v(2.7, -19.76) * mm, v(2.2, -20.64) * mm]});
            skFitSpline(sketch, "E263", {"points": [v(2.2, -20.64) * mm, v(1.72, -21.54) * mm, v(1.62, -22.46) * mm, v(1.87, -23.41) * mm]});
            skFitSpline(sketch, "E264", {"points": [v(1.87, -23.41) * mm, v(2.14, -24.37) * mm, v(2.72, -25.12) * mm, v(3.62, -25.6) * mm]});
            skFitSpline(sketch, "E265", {"points": [v(3.62, -25.6) * mm, v(4.52, -26.1) * mm, v(5.44, -26.22) * mm, v(6.37, -26) * mm]});
            skFitSpline(sketch, "E266", {"points": [v(6.37, -26) * mm, v(6.75, -25.84) * mm, v(6.87, -25.6) * mm, v(6.8, -25.22) * mm]});
            skFitSpline(sketch, "E267", {"points": [v(6.8, -25.22) * mm, v(6.77, -25.07) * mm, v(6.67, -24.94) * mm, v(6.47, -24.84) * mm]});
            skFitSpline(sketch, "E268", {"points": [v(6.47, -24.84) * mm, v(6.27, -24.74) * mm, v(6.07, -24.72) * mm, v(5.87, -24.77) * mm]});
            skFitSpline(sketch, "E269", {"points": [v(5.87, -24.77) * mm, v(5.3, -24.84) * mm, v(4.74, -24.7) * mm, v(4.24, -24.32) * mm]});
            skFitSpline(sketch, "E270", {"points": [v(4.24, -24.32) * mm, v(3.72, -23.94) * mm, v(3.42, -23.51) * mm, v(3.32, -23.01) * mm]});
            skFitSpline(sketch, "E271", {"points": [v(3.32, -23.01) * mm, v(3.22, -22.69) * mm, v(3.22, -22.29) * mm, v(3.34, -21.86) * mm]});
            skLineSegment(sketch, "E272", {"start": v(3.34, -21.86) * mm, "end": v(3.37, -21.79) * mm});
            skLineSegment(sketch, "E273", {"start": v(3.37, -21.79) * mm, "end": v(7.62, -24.12) * mm});
            skFitSpline(sketch, "E274", {"points": [v(7.62, -24.12) * mm, v(7.82, -24.22) * mm, v(8, -24.27) * mm, v(8.17, -24.22) * mm]});
            skFitSpline(sketch, "E275", {"points": [v(8.17, -24.22) * mm, v(8.35, -24.17) * mm, v(8.47, -24.06) * mm, v(8.57, -23.89) * mm]});
            skLineSegment(sketch, "E276", {"start": v(8.57, -23.89) * mm, "end": v(8.6, -23.81) * mm});
            skFitSpline(sketch, "E277", {"points": [v(8.6, -23.81) * mm, v(9.02, -22.91) * mm, v(9.1, -22.01) * mm, v(8.8, -21.14) * mm]});
            skFitSpline(sketch, "E278", {"points": [v(8.8, -21.14) * mm, v(8.52, -20.26) * mm, v(7.95, -19.59) * mm, v(7.1, -19.11) * mm]});
            skLineSegment(sketch, "E279", {"start": v(7.72, -22.79) * mm, "end": v(7.7, -22.86) * mm});
            skLineSegment(sketch, "E280", {"start": v(7.7, -22.86) * mm, "end": v(3.82, -20.76) * mm});
            skLineSegment(sketch, "E281", {"start": v(3.82, -20.76) * mm, "end": v(3.87, -20.71) * mm});
            skFitSpline(sketch, "E282", {"points": [v(3.87, -20.71) * mm, v(4.12, -20.41) * mm, v(4.47, -20.19) * mm, v(4.97, -20.06) * mm]});
            skFitSpline(sketch, "E283", {"points": [v(4.97, -20.06) * mm, v(5.44, -19.94) * mm, v(5.97, -20.01) * mm, v(6.5, -20.26) * mm]});
            skFitSpline(sketch, "E284", {"points": [v(6.5, -20.26) * mm, v(7, -20.59) * mm, v(7.37, -21.01) * mm, v(7.55, -21.51) * mm]});
            skFitSpline(sketch, "E285", {"points": [v(7.55, -21.51) * mm, v(7.77, -22.01) * mm, v(7.82, -22.44) * mm, v(7.72, -22.79) * mm]});
            skFitSpline(sketch, "E286", {"points": [v(15.83, -23.14) * mm, v(15.3, -22.94) * mm, v(14.75, -22.89) * mm, v(14.2, -23.01) * mm]});
            skLineSegment(sketch, "E287", {"start": v(14.2, -23.01) * mm, "end": v(14.13, -23.04) * mm});
            skLineSegment(sketch, "E288", {"start": v(14.13, -23.04) * mm, "end": v(14.13, -22.96) * mm});
            skFitSpline(sketch, "E289", {"points": [v(14.13, -22.96) * mm, v(14.1, -22.64) * mm, v(13.95, -22.44) * mm, v(13.65, -22.31) * mm]});
            skFitSpline(sketch, "E290", {"points": [v(13.65, -22.31) * mm, v(13.45, -22.24) * mm, v(13.28, -22.24) * mm, v(13.1, -22.34) * mm]});
            skFitSpline(sketch, "E291", {"points": [v(13.1, -22.34) * mm, v(12.93, -22.41) * mm, v(12.8, -22.56) * mm, v(12.72, -22.74) * mm]});
            skLineSegment(sketch, "E292", {"start": v(12.72, -22.74) * mm, "end": v(10.62, -28.27) * mm});
            skFitSpline(sketch, "E293", {"points": [v(10.62, -28.27) * mm, v(10.55, -28.47) * mm, v(10.55, -28.64) * mm, v(10.65, -28.82) * mm]});
            skFitSpline(sketch, "E294", {"points": [v(10.65, -28.82) * mm, v(10.72, -29) * mm, v(10.87, -29.12) * mm, v(11.05, -29.2) * mm]});
            skFitSpline(sketch, "E295", {"points": [v(11.05, -29.2) * mm, v(11.25, -29.27) * mm, v(11.42, -29.27) * mm, v(11.62, -29.2) * mm]});
            skFitSpline(sketch, "E296", {"points": [v(11.62, -29.2) * mm, v(11.82, -29.12) * mm, v(11.95, -29) * mm, v(12.02, -28.8) * mm]});
            skLineSegment(sketch, "E297", {"start": v(12.02, -28.8) * mm, "end": v(13.3, -25.44) * mm});
            skFitSpline(sketch, "E298", {"points": [v(13.3, -25.44) * mm, v(13.45, -25.04) * mm, v(13.73, -24.74) * mm, v(14.13, -24.57) * mm]});
            skFitSpline(sketch, "E299", {"points": [v(14.13, -24.57) * mm, v(14.33, -24.47) * mm, v(14.55, -24.42) * mm, v(14.75, -24.42) * mm]});
            skFitSpline(sketch, "E300", {"points": [v(14.75, -24.42) * mm, v(14.95, -24.42) * mm, v(15.13, -24.44) * mm, v(15.33, -24.52) * mm]});
            skFitSpline(sketch, "E301", {"points": [v(15.33, -24.52) * mm, v(15.73, -24.67) * mm, v(16.05, -24.97) * mm, v(16.23, -25.34) * mm]});
            skFitSpline(sketch, "E302", {"points": [v(16.23, -25.34) * mm, v(16.4, -25.74) * mm, v(16.43, -26.14) * mm, v(16.28, -26.57) * mm]});
            skLineSegment(sketch, "E303", {"start": v(16.28, -26.57) * mm, "end": v(15, -29.92) * mm});
            skFitSpline(sketch, "E304", {"points": [v(15, -29.92) * mm, v(14.93, -30.12) * mm, v(14.93, -30.3) * mm, v(15.03, -30.47) * mm]});
            skFitSpline(sketch, "E305", {"points": [v(15.03, -30.47) * mm, v(15.13, -30.67) * mm, v(15.25, -30.8) * mm, v(15.43, -30.84) * mm]});
            skFitSpline(sketch, "E306", {"points": [v(15.43, -30.84) * mm, v(15.6, -30.92) * mm, v(15.8, -30.92) * mm, v(15.98, -30.82) * mm]});
            skFitSpline(sketch, "E307", {"points": [v(15.98, -30.82) * mm, v(16.15, -30.74) * mm, v(16.28, -30.6) * mm, v(16.35, -30.42) * mm]});
            skLineSegment(sketch, "E308", {"start": v(16.35, -30.42) * mm, "end": v(17.63, -27.07) * mm});
            skFitSpline(sketch, "E309", {"points": [v(17.63, -27.07) * mm, v(17.93, -26.3) * mm, v(17.9, -25.52) * mm, v(17.55, -24.74) * mm]});
            skFitSpline(sketch, "E310", {"points": [v(17.55, -24.74) * mm, v(17.2, -23.99) * mm, v(16.63, -23.44) * mm, v(15.83, -23.14) * mm]});
            skFitSpline(sketch, "E311", {"points": [v(27.81, -23.56) * mm, v(27.61, -23.51) * mm, v(27.41, -23.54) * mm, v(27.24, -23.66) * mm]});
            skFitSpline(sketch, "E312", {"points": [v(27.24, -23.66) * mm, v(27.06, -23.76) * mm, v(26.93, -23.91) * mm, v(26.88, -24.12) * mm]});
            skLineSegment(sketch, "E313", {"start": v(26.88, -24.12) * mm, "end": v(26.2, -26.97) * mm});
            skLineSegment(sketch, "E314", {"start": v(26.2, -26.97) * mm, "end": v(26.13, -26.87) * mm});
            skFitSpline(sketch, "E315", {"points": [v(26.13, -26.87) * mm, v(25.66, -26.34) * mm, v(25.06, -25.97) * mm, v(24.36, -25.82) * mm]});
            skFitSpline(sketch, "E316", {"points": [v(24.36, -25.82) * mm, v(23.4, -25.6) * mm, v(22.48, -25.74) * mm, v(21.63, -26.3) * mm]});
            skFitSpline(sketch, "E317", {"points": [v(21.63, -26.3) * mm, v(20.78, -26.84) * mm, v(20.23, -27.62) * mm, v(20, -28.6) * mm]});
            skFitSpline(sketch, "E318", {"points": [v(20, -28.6) * mm, v(19.78, -29.57) * mm, v(19.9, -30.5) * mm, v(20.43, -31.37) * mm]});
            skFitSpline(sketch, "E319", {"points": [v(20.43, -31.37) * mm, v(20.93, -32.22) * mm, v(21.68, -32.8) * mm, v(22.66, -33.02) * mm]});
            skFitSpline(sketch, "E320", {"points": [v(22.66, -33.02) * mm, v(23.36, -33.2) * mm, v(24.06, -33.15) * mm, v(24.76, -32.87) * mm]});
            skLineSegment(sketch, "E321", {"start": v(24.76, -32.87) * mm, "end": v(24.83, -32.85) * mm});
            skLineSegment(sketch, "E322", {"start": v(24.83, -32.85) * mm, "end": v(24.83, -32.95) * mm});
            skFitSpline(sketch, "E323", {"points": [v(24.83, -32.95) * mm, v(24.83, -33.12) * mm, v(24.88, -33.27) * mm, v(24.98, -33.42) * mm]});
            skFitSpline(sketch, "E324", {"points": [v(24.98, -33.42) * mm, v(25.08, -33.57) * mm, v(25.23, -33.65) * mm, v(25.43, -33.7) * mm]});
            skFitSpline(sketch, "E325", {"points": [v(25.43, -33.7) * mm, v(25.63, -33.75) * mm, v(25.8, -33.72) * mm, v(25.98, -33.6) * mm]});
            skFitSpline(sketch, "E326", {"points": [v(25.98, -33.6) * mm, v(26.16, -33.5) * mm, v(26.28, -33.35) * mm, v(26.33, -33.15) * mm]});
            skLineSegment(sketch, "E327", {"start": v(26.33, -33.15) * mm, "end": v(28.41, -24.52) * mm});
            skFitSpline(sketch, "E328", {"points": [v(28.41, -24.52) * mm, v(28.46, -24.32) * mm, v(28.44, -24.14) * mm, v(28.31, -23.94) * mm]});
            skFitSpline(sketch, "E329", {"points": [v(28.31, -23.94) * mm, v(28.19, -23.71) * mm, v(28.04, -23.59) * mm, v(27.81, -23.56) * mm]});
            skFitSpline(sketch, "E330", {"points": [v(25.53, -29.9) * mm, v(25.4, -30.47) * mm, v(25.08, -30.92) * mm, v(24.58, -31.25) * mm]});
            skFitSpline(sketch, "E331", {"points": [v(24.58, -31.25) * mm, v(24.23, -31.47) * mm, v(23.86, -31.6) * mm, v(23.48, -31.6) * mm]});
            skFitSpline(sketch, "E332", {"points": [v(23.48, -31.6) * mm, v(23.33, -31.6) * mm, v(23.16, -31.57) * mm, v(23, -31.55) * mm]});
            skFitSpline(sketch, "E333", {"points": [v(23, -31.55) * mm, v(22.46, -31.42) * mm, v(22.03, -31.1) * mm, v(21.73, -30.57) * mm]});
            skFitSpline(sketch, "E334", {"points": [v(21.73, -30.57) * mm, v(21.43, -30.07) * mm, v(21.36, -29.52) * mm, v(21.48, -28.94) * mm]});
            skFitSpline(sketch, "E335", {"points": [v(21.48, -28.94) * mm, v(21.6, -28.37) * mm, v(21.93, -27.92) * mm, v(22.43, -27.6) * mm]});
            skFitSpline(sketch, "E336", {"points": [v(22.43, -27.6) * mm, v(22.93, -27.27) * mm, v(23.46, -27.17) * mm, v(24, -27.3) * mm]});
            skFitSpline(sketch, "E337", {"points": [v(24, -27.3) * mm, v(24.56, -27.42) * mm, v(25, -27.74) * mm, v(25.28, -28.27) * mm]});
            skFitSpline(sketch, "E338", {"points": [v(25.28, -28.27) * mm, v(25.58, -28.77) * mm, v(25.66, -29.32) * mm, v(25.53, -29.9) * mm]});
            skFitSpline(sketch, "E339", {"points": [v(36.74, -28.37) * mm, v(36.72, -28.34) * mm, v(36.72, -28.32) * mm, v(36.72, -28.27) * mm]});
            skFitSpline(sketch, "E340", {"points": [v(36.72, -28.27) * mm, v(36.72, -28.25) * mm, v(36.7, -28.2) * mm, v(36.7, -28.14) * mm]});
            skFitSpline(sketch, "E341", {"points": [v(36.7, -28.14) * mm, v(36.67, -28.12) * mm, v(36.64, -28.1) * mm, v(36.62, -28.04) * mm]});
            skFitSpline(sketch, "E342", {"points": [v(36.62, -28.04) * mm, v(36.6, -28.03) * mm, v(36.6, -28) * mm, v(36.6, -28) * mm]});
            skLineSegment(sketch, "E343", {"start": v(36.6, -28) * mm, "end": v(36.57, -28) * mm});
            skLineSegment(sketch, "E344", {"start": v(36.57, -28) * mm, "end": v(36.5, -27.87) * mm});
            skLineSegment(sketch, "E345", {"start": v(36.5, -27.87) * mm, "end": v(36.4, -27.8) * mm});
            skFitSpline(sketch, "E346", {"points": [v(36.4, -27.8) * mm, v(36.37, -27.8) * mm, v(36.34, -27.77) * mm, v(36.34, -27.74) * mm]});
            skFitSpline(sketch, "E347", {"points": [v(36.34, -27.74) * mm, v(36.32, -27.72) * mm, v(36.3, -27.72) * mm, v(36.27, -27.7) * mm]});
            skLineSegment(sketch, "E348", {"start": v(36.24, -27.7) * mm, "end": v(36.17, -27.7) * mm});
            skLineSegment(sketch, "E349", {"start": v(36.17, -27.7) * mm, "end": v(36.07, -27.67) * mm});
            skLineSegment(sketch, "E350", {"start": v(36.07, -27.67) * mm, "end": v(31.76, -27.22) * mm});
            skFitSpline(sketch, "E351", {"points": [v(31.76, -27.22) * mm, v(31.56, -27.2) * mm, v(31.39, -27.24) * mm, v(31.24, -27.37) * mm]});
            skFitSpline(sketch, "E352", {"points": [v(31.24, -27.37) * mm, v(31.06, -27.5) * mm, v(30.99, -27.67) * mm, v(30.96, -27.87) * mm]});
            skFitSpline(sketch, "E353", {"points": [v(30.96, -27.87) * mm, v(30.94, -28.07) * mm, v(30.99, -28.24) * mm, v(31.14, -28.4) * mm]});
            skFitSpline(sketch, "E354", {"points": [v(31.14, -28.4) * mm, v(31.26, -28.54) * mm, v(31.44, -28.64) * mm, v(31.61, -28.67) * mm]});
            skLineSegment(sketch, "E355", {"start": v(31.61, -28.67) * mm, "end": v(34.47, -28.97) * mm});
            skLineSegment(sketch, "E356", {"start": v(34.47, -28.97) * mm, "end": v(30.54, -33.4) * mm});
            skLineSegment(sketch, "E357", {"start": v(30.54, -33.4) * mm, "end": v(30.51, -33.4) * mm});
            skLineSegment(sketch, "E358", {"start": v(30.51, -33.4) * mm, "end": v(30.51, -33.45) * mm});
            skLineSegment(sketch, "E359", {"start": v(30.51, -33.45) * mm, "end": v(30.49, -33.45) * mm});
            skFitSpline(sketch, "E360", {"points": [v(30.49, -33.45) * mm, v(30.45, -33.46) * mm, v(30.44, -33.49) * mm, v(30.44, -33.52) * mm]});
            skFitSpline(sketch, "E361", {"points": [v(30.44, -33.52) * mm, v(30.44, -33.57) * mm, v(30.41, -33.6) * mm, v(30.39, -33.62) * mm]});
            skLineSegment(sketch, "E362", {"start": v(30.39, -33.62) * mm, "end": v(30.39, -33.67) * mm});
            skLineSegment(sketch, "E363", {"start": v(30.39, -33.67) * mm, "end": v(30.36, -33.77) * mm});
            skLineSegment(sketch, "E364", {"start": v(30.36, -33.77) * mm, "end": v(30.39, -33.8) * mm});
            skLineSegment(sketch, "E365", {"start": v(30.39, -33.8) * mm, "end": v(30.39, -33.92) * mm});
            skLineSegment(sketch, "E366", {"start": v(30.39, -33.92) * mm, "end": v(30.41, -34.07) * mm});
            skLineSegment(sketch, "E367", {"start": v(30.41, -34.07) * mm, "end": v(30.46, -34.12) * mm});
            skLineSegment(sketch, "E368", {"start": v(30.46, -34.12) * mm, "end": v(30.46, -34.17) * mm});
            skFitSpline(sketch, "E369", {"points": [v(30.46, -34.17) * mm, v(30.46, -34.19) * mm, v(30.49, -34.23) * mm, v(30.54, -34.3) * mm]});
            skFitSpline(sketch, "E370", {"points": [v(30.54, -34.3) * mm, v(30.57, -34.36) * mm, v(30.6, -34.4) * mm, v(30.64, -34.4) * mm]});
            skLineSegment(sketch, "E371", {"start": v(30.64, -34.4) * mm, "end": v(30.71, -34.4) * mm});
            skLineSegment(sketch, "E372", {"start": v(30.71, -34.4) * mm, "end": v(30.71, -34.45) * mm});
            skLineSegment(sketch, "E373", {"start": v(30.74, -34.47) * mm, "end": v(30.84, -34.52) * mm});
            skFitSpline(sketch, "E374", {"points": [v(30.84, -34.52) * mm, v(30.85, -34.52) * mm, v(30.88, -34.53) * mm, v(30.91, -34.55) * mm]});
            skLineSegment(sketch, "E375", {"start": v(30.91, -34.55) * mm, "end": v(30.94, -34.55) * mm});
            skFitSpline(sketch, "E376", {"points": [v(30.94, -34.55) * mm, v(30.99, -34.57) * mm, v(31.04, -34.57) * mm, v(31.09, -34.57) * mm]});
            skLineSegment(sketch, "E377", {"start": v(31.09, -34.57) * mm, "end": v(35.4, -35.02) * mm});
            skFitSpline(sketch, "E378", {"points": [v(35.4, -35.02) * mm, v(35.6, -35.05) * mm, v(35.77, -35) * mm, v(35.92, -34.87) * mm]});
            skFitSpline(sketch, "E379", {"points": [v(35.92, -34.87) * mm, v(36.1, -34.75) * mm, v(36.17, -34.57) * mm, v(36.2, -34.37) * mm]});
            skFitSpline(sketch, "E380", {"points": [v(36.2, -34.37) * mm, v(36.22, -34.17) * mm, v(36.17, -34) * mm, v(36.02, -33.85) * mm]});
            skFitSpline(sketch, "E381", {"points": [v(36.02, -33.85) * mm, v(35.9, -33.7) * mm, v(35.72, -33.6) * mm, v(35.54, -33.57) * mm]});
            skLineSegment(sketch, "E382", {"start": v(35.54, -33.57) * mm, "end": v(32.66, -33.27) * mm});
            skLineSegment(sketch, "E383", {"start": v(32.66, -33.27) * mm, "end": v(36.6, -28.87) * mm});
            skLineSegment(sketch, "E384", {"start": v(36.6, -28.87) * mm, "end": v(36.64, -28.82) * mm});
            skLineSegment(sketch, "E385", {"start": v(36.64, -28.82) * mm, "end": v(36.64, -28.74) * mm});
            skLineSegment(sketch, "E386", {"start": v(36.64, -28.74) * mm, "end": v(36.7, -28.74) * mm});
            skLineSegment(sketch, "E387", {"start": v(36.7, -28.74) * mm, "end": v(36.7, -28.7) * mm});
            skFitSpline(sketch, "E388", {"points": [v(36.7, -28.7) * mm, v(36.72, -28.67) * mm, v(36.72, -28.62) * mm, v(36.72, -28.57) * mm]});
            skLineSegment(sketch, "E389", {"start": v(36.72, -28.57) * mm, "end": v(36.74, -28.5) * mm});
            skLineSegment(sketch, "E390", {"start": v(36.74, -28.5) * mm, "end": v(36.74, -28.44) * mm});
            skLineSegment(sketch, "E391", {"start": v(36.74, -28.44) * mm, "end": v(36.74, -28.37) * mm});
            skArc(sketch, "E392", {"start": v(-39.94, 40.51) * mm, "mid": v(-16.5, -16.05) * mm, "end": v(40.06, -39.49) * mm});
            skLineSegment(sketch, "E393", {"start": v(30.71, -34.45) * mm, "end": v(30.73, -34.47) * mm});
            skLineSegment(sketch, "E394", {"start": v(30.73, -34.47) * mm, "end": v(30.74, -34.47) * mm});
            skLineSegment(sketch, "E395", {"start": v(-39.94, 40.51) * mm, "end": v(40.06, 40.51) * mm});
            skLineSegment(sketch, "E396", {"start": v(40.06, 40.51) * mm, "end": v(40.06, -39.49) * mm});
            skLineSegment(sketch, "E397", {"start": v(36.24, -27.7) * mm, "end": v(36.27, -27.7) * mm});
            skLineSegment(sketch, "E398", {"start": v(30.84, -34.52) * mm, "end": v(30.84, -34.52) * mm});
            skSolve(sketch);
        }
        {
            var Q0;
            Q0 = qSketchRegion(id + "F0", true);
            var Q1;
            Q1=makeQuery(id+"F0.imprint","IMPRINT",FACE,{"disambiguationData":[TD([[makeQuery(id+"F0.imprint","IMPRINT",EDGE,{"derivedFrom":sQuery(id+"F0.wireOp",EDGE,"E41")}),1.0]])]});
            var Q2;
            Q2=makeQuery(id+"F0.imprint","IMPRINT",FACE,{"disambiguationData":[TD([[makeQuery(id+"F0.imprint","IMPRINT",EDGE,{"derivedFrom":sQuery(id+"F0.wireOp",EDGE,"E78")}),1.0]])]});
            var Q3;
            Q3=makeQuery(id+"F0.imprint","IMPRINT",FACE,{"disambiguationData":[TD([[makeQuery(id+"F0.imprint","IMPRINT",EDGE,{"derivedFrom":sQuery(id+"F0.wireOp",EDGE,"E118")}),1.0]])]});
            var Q4;
            Q4=makeQuery(id+"F0.imprint","IMPRINT",FACE,{"disambiguationData":[TD([[makeQuery(id+"F0.imprint","IMPRINT",EDGE,{"derivedFrom":sQuery(id+"F0.wireOp",EDGE,"E134")}),-1.0]])]});
            var Q5;
            Q5=makeQuery(id+"F0.imprint","IMPRINT",FACE,{"disambiguationData":[TD([[makeQuery(id+"F0.imprint","IMPRINT",EDGE,{"derivedFrom":sQuery(id+"F0.wireOp",EDGE,"E21")}),1.0]])]});
            var Q6;
            Q6=makeQuery(id+"F0.imprint","IMPRINT",FACE,{"disambiguationData":[TD([[makeQuery(id+"F0.imprint","IMPRINT",EDGE,{"derivedFrom":sQuery(id+"F0.wireOp",EDGE,"E0")}),1.0]])]});
            var Q7;
            Q7=makeQuery(id+"F0.imprint","IMPRINT",FACE,{"disambiguationData":[TD([[makeQuery(id+"F0.imprint","IMPRINT",EDGE,{"derivedFrom":sQuery(id+"F0.wireOp",EDGE,"E143")}),1.0]])]});
            var Q8;
            Q8=makeQuery(id+"F0.imprint","IMPRINT",FACE,{"disambiguationData":[TD([[makeQuery(id+"F0.imprint","IMPRINT",EDGE,{"derivedFrom":sQuery(id+"F0.wireOp",EDGE,"E161")}),1.0]])]});
            var Q9;
            Q9=makeQuery(id+"F0.imprint","IMPRINT",FACE,{"disambiguationData":[TD([[makeQuery(id+"F0.imprint","IMPRINT",EDGE,{"derivedFrom":sQuery(id+"F0.wireOp",EDGE,"E188")}),1.0]])]});
            var Q10;
            Q10=makeQuery(id+"F0.imprint","IMPRINT",FACE,{"disambiguationData":[TD([[makeQuery(id+"F0.imprint","IMPRINT",EDGE,{"derivedFrom":sQuery(id+"F0.wireOp",EDGE,"E218")}),1.0]])]});
            var Q11;
            Q11=makeQuery(id+"F0.imprint","IMPRINT",FACE,{"disambiguationData":[TD([[makeQuery(id+"F0.imprint","IMPRINT",EDGE,{"derivedFrom":sQuery(id+"F0.wireOp",EDGE,"E238")}),1.0]])]});
            var Q12;
            Q12=makeQuery(id+"F0.imprint","IMPRINT",FACE,{"disambiguationData":[TD([[makeQuery(id+"F0.imprint","IMPRINT",EDGE,{"derivedFrom":sQuery(id+"F0.wireOp",EDGE,"E249")}),1.0]])]});
            var Q13;
            Q13=makeQuery(id+"F0.imprint","IMPRINT",FACE,{"disambiguationData":[TD([[makeQuery(id+"F0.imprint","IMPRINT",EDGE,{"derivedFrom":sQuery(id+"F0.wireOp",EDGE,"E260")}),1.0]])]});
            var Q14;
            Q14=makeQuery(id+"F0.imprint","IMPRINT",FACE,{"disambiguationData":[TD([[makeQuery(id+"F0.imprint","IMPRINT",EDGE,{"derivedFrom":sQuery(id+"F0.wireOp",EDGE,"E279")}),-1.0]])]});
            var Q15;
            Q15=makeQuery(id+"F0.imprint","IMPRINT",FACE,{"disambiguationData":[TD([[makeQuery(id+"F0.imprint","IMPRINT",EDGE,{"derivedFrom":sQuery(id+"F0.wireOp",EDGE,"E286")}),1.0]])]});
            var Q16;
            Q16=makeQuery(id+"F0.imprint","IMPRINT",FACE,{"disambiguationData":[TD([[makeQuery(id+"F0.imprint","IMPRINT",EDGE,{"derivedFrom":sQuery(id+"F0.wireOp",EDGE,"E330")}),-1.0]])]});
            var Q17;
            Q17=makeQuery(id+"F0.imprint","IMPRINT",FACE,{"disambiguationData":[TD([[makeQuery(id+"F0.imprint","IMPRINT",EDGE,{"derivedFrom":sQuery(id+"F0.wireOp",EDGE,"E311")}),1.0]])]});
            var Q18;
            Q18=makeQuery(id+"F0.imprint","IMPRINT",FACE,{"disambiguationData":[TD([[makeQuery(id+"F0.imprint","IMPRINT",EDGE,{"derivedFrom":sQuery(id+"F0.wireOp",EDGE,"E339")}),1.0]])]});
            extrude(context, id + "F1", {"entities" : qUnion([Q0, Q1, Q2, Q3, Q4, Q5, Q6, Q7, Q8, Q9, Q10, Q11, Q12, Q13, Q14, Q15, Q16, Q17, Q18]), "oppositeDirection" : true, "depth" : 2 * mm});
        }
        {
            var Q0;
            Q0=makeQuery(id+"F0.imprint","IMPRINT",FACE,{"disambiguationData":[TD([[makeQuery(id+"F0.imprint","IMPRINT",EDGE,{"derivedFrom":sQuery(id+"F0.wireOp",EDGE,"E0")}),-1.0]])]});
            var Q1;
            Q1=makeQuery(id+"F0.imprint","IMPRINT",FACE,{"disambiguationData":[TD([[makeQuery(id+"F0.imprint","IMPRINT",EDGE,{"derivedFrom":sQuery(id+"F0.wireOp",EDGE,"E330")}),-1.0]])]});
            var Q2;
            Q2=makeQuery(id+"F0.imprint","IMPRINT",FACE,{"disambiguationData":[TD([[makeQuery(id+"F0.imprint","IMPRINT",EDGE,{"derivedFrom":sQuery(id+"F0.wireOp",EDGE,"E279")}),-1.0]])]});
            var Q3;
            Q3=makeQuery(id+"F0.imprint","IMPRINT",FACE,{"disambiguationData":[TD([[makeQuery(id+"F0.imprint","IMPRINT",EDGE,{"derivedFrom":sQuery(id+"F0.wireOp",EDGE,"E134")}),-1.0]])]});
            extrude(context, id + "F2", {"entities" : qUnion([Q0, Q1, Q2, Q3]), "operationType" : NewBodyOperationType.ADD, "depth" : 2 * mm});
        }
        {
            var Q0;
            Q0=makeQuery(id+"F2.opExtrude","CAP_FACE",FACE,{"disambiguationData":[OSD([sQuery(id+"F0.wireOp",EDGE,"E0"),sQuery(id+"F0.wireOp",EDGE,"E1"),sQuery(id+"F0.wireOp",EDGE,"E2"),sQuery(id+"F0.wireOp",EDGE,"E3"),sQuery(id+"F0.wireOp",EDGE,"E4"),sQuery(id+"F0.wireOp",EDGE,"E5"),sQuery(id+"F0.wireOp",EDGE,"E6"),sQuery(id+"F0.wireOp",EDGE,"E7"),sQuery(id+"F0.wireOp",EDGE,"E8"),sQuery(id+"F0.wireOp",EDGE,"E9"),sQuery(id+"F0.wireOp",EDGE,"E10"),sQuery(id+"F0.wireOp",EDGE,"E11"),sQuery(id+"F0.wireOp",EDGE,"E12"),sQuery(id+"F0.wireOp",EDGE,"E13"),sQuery(id+"F0.wireOp",EDGE,"E14"),sQuery(id+"F0.wireOp",EDGE,"E15"),sQuery(id+"F0.wireOp",EDGE,"E16"),sQuery(id+"F0.wireOp",EDGE,"E17"),sQuery(id+"F0.wireOp",EDGE,"E18"),sQuery(id+"F0.wireOp",EDGE,"E19"),sQuery(id+"F0.wireOp",EDGE,"E20"),sQuery(id+"F0.wireOp",EDGE,"E21"),sQuery(id+"F0.wireOp",EDGE,"E22"),sQuery(id+"F0.wireOp",EDGE,"E23"),sQuery(id+"F0.wireOp",EDGE,"E24"),sQuery(id+"F0.wireOp",EDGE,"E25"),sQuery(id+"F0.wireOp",EDGE,"E26"),sQuery(id+"F0.wireOp",EDGE,"E27"),sQuery(id+"F0.wireOp",EDGE,"E28"),sQuery(id+"F0.wireOp",EDGE,"E29"),sQuery(id+"F0.wireOp",EDGE,"E30"),sQuery(id+"F0.wireOp",EDGE,"E31"),sQuery(id+"F0.wireOp",EDGE,"E32"),sQuery(id+"F0.wireOp",EDGE,"E33"),sQuery(id+"F0.wireOp",EDGE,"E34"),sQuery(id+"F0.wireOp",EDGE,"E35"),sQuery(id+"F0.wireOp",EDGE,"E36"),sQuery(id+"F0.wireOp",EDGE,"E37"),sQuery(id+"F0.wireOp",EDGE,"E38"),sQuery(id+"F0.wireOp",EDGE,"E39"),sQuery(id+"F0.wireOp",EDGE,"E40"),sQuery(id+"F0.wireOp",EDGE,"E41"),sQuery(id+"F0.wireOp",EDGE,"E42"),sQuery(id+"F0.wireOp",EDGE,"E43"),sQuery(id+"F0.wireOp",EDGE,"E44"),sQuery(id+"F0.wireOp",EDGE,"E45"),sQuery(id+"F0.wireOp",EDGE,"E46"),sQuery(id+"F0.wireOp",EDGE,"E47"),sQuery(id+"F0.wireOp",EDGE,"E48"),sQuery(id+"F0.wireOp",EDGE,"E49"),sQuery(id+"F0.wireOp",EDGE,"E50"),sQuery(id+"F0.wireOp",EDGE,"E51"),sQuery(id+"F0.wireOp",EDGE,"E52"),sQuery(id+"F0.wireOp",EDGE,"E53"),sQuery(id+"F0.wireOp",EDGE,"E54"),sQuery(id+"F0.wireOp",EDGE,"E55"),sQuery(id+"F0.wireOp",EDGE,"E56"),sQuery(id+"F0.wireOp",EDGE,"E57"),sQuery(id+"F0.wireOp",EDGE,"E58"),sQuery(id+"F0.wireOp",EDGE,"E59"),sQuery(id+"F0.wireOp",EDGE,"E60"),sQuery(id+"F0.wireOp",EDGE,"E61"),sQuery(id+"F0.wireOp",EDGE,"E62"),sQuery(id+"F0.wireOp",EDGE,"E63"),sQuery(id+"F0.wireOp",EDGE,"E64"),sQuery(id+"F0.wireOp",EDGE,"E65"),sQuery(id+"F0.wireOp",EDGE,"E66"),sQuery(id+"F0.wireOp",EDGE,"E67"),sQuery(id+"F0.wireOp",EDGE,"E68"),sQuery(id+"F0.wireOp",EDGE,"E69"),sQuery(id+"F0.wireOp",EDGE,"E70"),sQuery(id+"F0.wireOp",EDGE,"E71"),sQuery(id+"F0.wireOp",EDGE,"E72"),sQuery(id+"F0.wireOp",EDGE,"E73"),sQuery(id+"F0.wireOp",EDGE,"E74"),sQuery(id+"F0.wireOp",EDGE,"E75"),sQuery(id+"F0.wireOp",EDGE,"E76"),sQuery(id+"F0.wireOp",EDGE,"E77"),sQuery(id+"F0.wireOp",EDGE,"E78"),sQuery(id+"F0.wireOp",EDGE,"E79"),sQuery(id+"F0.wireOp",EDGE,"E80"),sQuery(id+"F0.wireOp",EDGE,"E81"),sQuery(id+"F0.wireOp",EDGE,"E82"),sQuery(id+"F0.wireOp",EDGE,"E83"),sQuery(id+"F0.wireOp",EDGE,"E84"),sQuery(id+"F0.wireOp",EDGE,"E85"),sQuery(id+"F0.wireOp",EDGE,"E86"),sQuery(id+"F0.wireOp",EDGE,"E87"),sQuery(id+"F0.wireOp",EDGE,"E88"),sQuery(id+"F0.wireOp",EDGE,"E89"),sQuery(id+"F0.wireOp",EDGE,"E90"),sQuery(id+"F0.wireOp",EDGE,"E91"),sQuery(id+"F0.wireOp",EDGE,"E92"),sQuery(id+"F0.wireOp",EDGE,"E93"),sQuery(id+"F0.wireOp",EDGE,"E94"),sQuery(id+"F0.wireOp",EDGE,"E95"),sQuery(id+"F0.wireOp",EDGE,"E96"),sQuery(id+"F0.wireOp",EDGE,"E97"),sQuery(id+"F0.wireOp",EDGE,"E98"),sQuery(id+"F0.wireOp",EDGE,"E99"),sQuery(id+"F0.wireOp",EDGE,"E100"),sQuery(id+"F0.wireOp",EDGE,"E101"),sQuery(id+"F0.wireOp",EDGE,"E102"),sQuery(id+"F0.wireOp",EDGE,"E103"),sQuery(id+"F0.wireOp",EDGE,"E104"),sQuery(id+"F0.wireOp",EDGE,"E105"),sQuery(id+"F0.wireOp",EDGE,"E106"),sQuery(id+"F0.wireOp",EDGE,"E107"),sQuery(id+"F0.wireOp",EDGE,"E108"),sQuery(id+"F0.wireOp",EDGE,"E109"),sQuery(id+"F0.wireOp",EDGE,"E110"),sQuery(id+"F0.wireOp",EDGE,"E111"),sQuery(id+"F0.wireOp",EDGE,"E112"),sQuery(id+"F0.wireOp",EDGE,"E113"),sQuery(id+"F0.wireOp",EDGE,"E114"),sQuery(id+"F0.wireOp",EDGE,"E115"),sQuery(id+"F0.wireOp",EDGE,"E116"),sQuery(id+"F0.wireOp",EDGE,"E117"),sQuery(id+"F0.wireOp",EDGE,"E118"),sQuery(id+"F0.wireOp",EDGE,"E119"),sQuery(id+"F0.wireOp",EDGE,"E120"),sQuery(id+"F0.wireOp",EDGE,"E121"),sQuery(id+"F0.wireOp",EDGE,"E122"),sQuery(id+"F0.wireOp",EDGE,"E123"),sQuery(id+"F0.wireOp",EDGE,"E124"),sQuery(id+"F0.wireOp",EDGE,"E125"),sQuery(id+"F0.wireOp",EDGE,"E126"),sQuery(id+"F0.wireOp",EDGE,"E127"),sQuery(id+"F0.wireOp",EDGE,"E128"),sQuery(id+"F0.wireOp",EDGE,"E129"),sQuery(id+"F0.wireOp",EDGE,"E130"),sQuery(id+"F0.wireOp",EDGE,"E131"),sQuery(id+"F0.wireOp",EDGE,"E132"),sQuery(id+"F0.wireOp",EDGE,"E133"),sQuery(id+"F0.wireOp",EDGE,"E143"),sQuery(id+"F0.wireOp",EDGE,"E144"),sQuery(id+"F0.wireOp",EDGE,"E145"),sQuery(id+"F0.wireOp",EDGE,"E146"),sQuery(id+"F0.wireOp",EDGE,"E147"),sQuery(id+"F0.wireOp",EDGE,"E148"),sQuery(id+"F0.wireOp",EDGE,"E149"),sQuery(id+"F0.wireOp",EDGE,"E150"),sQuery(id+"F0.wireOp",EDGE,"E151"),sQuery(id+"F0.wireOp",EDGE,"E152"),sQuery(id+"F0.wireOp",EDGE,"E153"),sQuery(id+"F0.wireOp",EDGE,"E154"),sQuery(id+"F0.wireOp",EDGE,"E155"),sQuery(id+"F0.wireOp",EDGE,"E156"),sQuery(id+"F0.wireOp",EDGE,"E157"),sQuery(id+"F0.wireOp",EDGE,"E158"),sQuery(id+"F0.wireOp",EDGE,"E159"),sQuery(id+"F0.wireOp",EDGE,"E160"),sQuery(id+"F0.wireOp",EDGE,"E161"),sQuery(id+"F0.wireOp",EDGE,"E162"),sQuery(id+"F0.wireOp",EDGE,"E163"),sQuery(id+"F0.wireOp",EDGE,"E164"),sQuery(id+"F0.wireOp",EDGE,"E165"),sQuery(id+"F0.wireOp",EDGE,"E166"),sQuery(id+"F0.wireOp",EDGE,"E167"),sQuery(id+"F0.wireOp",EDGE,"E168"),sQuery(id+"F0.wireOp",EDGE,"E169"),sQuery(id+"F0.wireOp",EDGE,"E170"),sQuery(id+"F0.wireOp",EDGE,"E171"),sQuery(id+"F0.wireOp",EDGE,"E172"),sQuery(id+"F0.wireOp",EDGE,"E173"),sQuery(id+"F0.wireOp",EDGE,"E174"),sQuery(id+"F0.wireOp",EDGE,"E175"),sQuery(id+"F0.wireOp",EDGE,"E176"),sQuery(id+"F0.wireOp",EDGE,"E177"),sQuery(id+"F0.wireOp",EDGE,"E178"),sQuery(id+"F0.wireOp",EDGE,"E179"),sQuery(id+"F0.wireOp",EDGE,"E180"),sQuery(id+"F0.wireOp",EDGE,"E181"),sQuery(id+"F0.wireOp",EDGE,"E182"),sQuery(id+"F0.wireOp",EDGE,"E183"),sQuery(id+"F0.wireOp",EDGE,"E184"),sQuery(id+"F0.wireOp",EDGE,"E185"),sQuery(id+"F0.wireOp",EDGE,"E186"),sQuery(id+"F0.wireOp",EDGE,"E187"),sQuery(id+"F0.wireOp",EDGE,"E188"),sQuery(id+"F0.wireOp",EDGE,"E189"),sQuery(id+"F0.wireOp",EDGE,"E190"),sQuery(id+"F0.wireOp",EDGE,"E191"),sQuery(id+"F0.wireOp",EDGE,"E192"),sQuery(id+"F0.wireOp",EDGE,"E193"),sQuery(id+"F0.wireOp",EDGE,"E194"),sQuery(id+"F0.wireOp",EDGE,"E195"),sQuery(id+"F0.wireOp",EDGE,"E196"),sQuery(id+"F0.wireOp",EDGE,"E197"),sQuery(id+"F0.wireOp",EDGE,"E198"),sQuery(id+"F0.wireOp",EDGE,"E199"),sQuery(id+"F0.wireOp",EDGE,"E200"),sQuery(id+"F0.wireOp",EDGE,"E201"),sQuery(id+"F0.wireOp",EDGE,"E202"),sQuery(id+"F0.wireOp",EDGE,"E203"),sQuery(id+"F0.wireOp",EDGE,"E204"),sQuery(id+"F0.wireOp",EDGE,"E205"),sQuery(id+"F0.wireOp",EDGE,"E206"),sQuery(id+"F0.wireOp",EDGE,"E207"),sQuery(id+"F0.wireOp",EDGE,"E208"),sQuery(id+"F0.wireOp",EDGE,"E209"),sQuery(id+"F0.wireOp",EDGE,"E210"),sQuery(id+"F0.wireOp",EDGE,"E211"),sQuery(id+"F0.wireOp",EDGE,"E212"),sQuery(id+"F0.wireOp",EDGE,"E213"),sQuery(id+"F0.wireOp",EDGE,"E214"),sQuery(id+"F0.wireOp",EDGE,"E215"),sQuery(id+"F0.wireOp",EDGE,"E216"),sQuery(id+"F0.wireOp",EDGE,"E217"),sQuery(id+"F0.wireOp",EDGE,"E218"),sQuery(id+"F0.wireOp",EDGE,"E219"),sQuery(id+"F0.wireOp",EDGE,"E220"),sQuery(id+"F0.wireOp",EDGE,"E221"),sQuery(id+"F0.wireOp",EDGE,"E222"),sQuery(id+"F0.wireOp",EDGE,"E223"),sQuery(id+"F0.wireOp",EDGE,"E224"),sQuery(id+"F0.wireOp",EDGE,"E225"),sQuery(id+"F0.wireOp",EDGE,"E226"),sQuery(id+"F0.wireOp",EDGE,"E227"),sQuery(id+"F0.wireOp",EDGE,"E228"),sQuery(id+"F0.wireOp",EDGE,"E229"),sQuery(id+"F0.wireOp",EDGE,"E230"),sQuery(id+"F0.wireOp",EDGE,"E231"),sQuery(id+"F0.wireOp",EDGE,"E232"),sQuery(id+"F0.wireOp",EDGE,"E233"),sQuery(id+"F0.wireOp",EDGE,"E234"),sQuery(id+"F0.wireOp",EDGE,"E235"),sQuery(id+"F0.wireOp",EDGE,"E236"),sQuery(id+"F0.wireOp",EDGE,"E237"),sQuery(id+"F0.wireOp",EDGE,"E238"),sQuery(id+"F0.wireOp",EDGE,"E239"),sQuery(id+"F0.wireOp",EDGE,"E240"),sQuery(id+"F0.wireOp",EDGE,"E241"),sQuery(id+"F0.wireOp",EDGE,"E242"),sQuery(id+"F0.wireOp",EDGE,"E243"),sQuery(id+"F0.wireOp",EDGE,"E244"),sQuery(id+"F0.wireOp",EDGE,"E245"),sQuery(id+"F0.wireOp",EDGE,"E246"),sQuery(id+"F0.wireOp",EDGE,"E247"),sQuery(id+"F0.wireOp",EDGE,"E248"),sQuery(id+"F0.wireOp",EDGE,"E249"),sQuery(id+"F0.wireOp",EDGE,"E250"),sQuery(id+"F0.wireOp",EDGE,"E251"),sQuery(id+"F0.wireOp",EDGE,"E252"),sQuery(id+"F0.wireOp",EDGE,"E253"),sQuery(id+"F0.wireOp",EDGE,"E254"),sQuery(id+"F0.wireOp",EDGE,"E255"),sQuery(id+"F0.wireOp",EDGE,"E256"),sQuery(id+"F0.wireOp",EDGE,"E257"),sQuery(id+"F0.wireOp",EDGE,"E258"),sQuery(id+"F0.wireOp",EDGE,"E259"),sQuery(id+"F0.wireOp",EDGE,"E260"),sQuery(id+"F0.wireOp",EDGE,"E261"),sQuery(id+"F0.wireOp",EDGE,"E262"),sQuery(id+"F0.wireOp",EDGE,"E263"),sQuery(id+"F0.wireOp",EDGE,"E264"),sQuery(id+"F0.wireOp",EDGE,"E265"),sQuery(id+"F0.wireOp",EDGE,"E266"),sQuery(id+"F0.wireOp",EDGE,"E267"),sQuery(id+"F0.wireOp",EDGE,"E268"),sQuery(id+"F0.wireOp",EDGE,"E269"),sQuery(id+"F0.wireOp",EDGE,"E270"),sQuery(id+"F0.wireOp",EDGE,"E271"),sQuery(id+"F0.wireOp",EDGE,"E272"),sQuery(id+"F0.wireOp",EDGE,"E273"),sQuery(id+"F0.wireOp",EDGE,"E274"),sQuery(id+"F0.wireOp",EDGE,"E275"),sQuery(id+"F0.wireOp",EDGE,"E276"),sQuery(id+"F0.wireOp",EDGE,"E277"),sQuery(id+"F0.wireOp",EDGE,"E278"),sQuery(id+"F0.wireOp",EDGE,"E286"),sQuery(id+"F0.wireOp",EDGE,"E287"),sQuery(id+"F0.wireOp",EDGE,"E288"),sQuery(id+"F0.wireOp",EDGE,"E289"),sQuery(id+"F0.wireOp",EDGE,"E290"),sQuery(id+"F0.wireOp",EDGE,"E291"),sQuery(id+"F0.wireOp",EDGE,"E292"),sQuery(id+"F0.wireOp",EDGE,"E293"),sQuery(id+"F0.wireOp",EDGE,"E294"),sQuery(id+"F0.wireOp",EDGE,"E295"),sQuery(id+"F0.wireOp",EDGE,"E296"),sQuery(id+"F0.wireOp",EDGE,"E297"),sQuery(id+"F0.wireOp",EDGE,"E298"),sQuery(id+"F0.wireOp",EDGE,"E299"),sQuery(id+"F0.wireOp",EDGE,"E300"),sQuery(id+"F0.wireOp",EDGE,"E301"),sQuery(id+"F0.wireOp",EDGE,"E302"),sQuery(id+"F0.wireOp",EDGE,"E303"),sQuery(id+"F0.wireOp",EDGE,"E304"),sQuery(id+"F0.wireOp",EDGE,"E305"),sQuery(id+"F0.wireOp",EDGE,"E306"),sQuery(id+"F0.wireOp",EDGE,"E307"),sQuery(id+"F0.wireOp",EDGE,"E308"),sQuery(id+"F0.wireOp",EDGE,"E309"),sQuery(id+"F0.wireOp",EDGE,"E310"),sQuery(id+"F0.wireOp",EDGE,"E311"),sQuery(id+"F0.wireOp",EDGE,"E312"),sQuery(id+"F0.wireOp",EDGE,"E313"),sQuery(id+"F0.wireOp",EDGE,"E314"),sQuery(id+"F0.wireOp",EDGE,"E315"),sQuery(id+"F0.wireOp",EDGE,"E316"),sQuery(id+"F0.wireOp",EDGE,"E317"),sQuery(id+"F0.wireOp",EDGE,"E318"),sQuery(id+"F0.wireOp",EDGE,"E319"),sQuery(id+"F0.wireOp",EDGE,"E320"),sQuery(id+"F0.wireOp",EDGE,"E321"),sQuery(id+"F0.wireOp",EDGE,"E322"),sQuery(id+"F0.wireOp",EDGE,"E323"),sQuery(id+"F0.wireOp",EDGE,"E324"),sQuery(id+"F0.wireOp",EDGE,"E325"),sQuery(id+"F0.wireOp",EDGE,"E326"),sQuery(id+"F0.wireOp",EDGE,"E327"),sQuery(id+"F0.wireOp",EDGE,"E328"),sQuery(id+"F0.wireOp",EDGE,"E329"),sQuery(id+"F0.wireOp",EDGE,"E339"),sQuery(id+"F0.wireOp",EDGE,"E340"),sQuery(id+"F0.wireOp",EDGE,"E341"),sQuery(id+"F0.wireOp",EDGE,"E342"),sQuery(id+"F0.wireOp",EDGE,"E343"),sQuery(id+"F0.wireOp",EDGE,"E344"),sQuery(id+"F0.wireOp",EDGE,"E345"),sQuery(id+"F0.wireOp",EDGE,"E346"),sQuery(id+"F0.wireOp",EDGE,"E347"),sQuery(id+"F0.wireOp",EDGE,"E348"),sQuery(id+"F0.wireOp",EDGE,"E349"),sQuery(id+"F0.wireOp",EDGE,"E350"),sQuery(id+"F0.wireOp",EDGE,"E351"),sQuery(id+"F0.wireOp",EDGE,"E352"),sQuery(id+"F0.wireOp",EDGE,"E353"),sQuery(id+"F0.wireOp",EDGE,"E354"),sQuery(id+"F0.wireOp",EDGE,"E355"),sQuery(id+"F0.wireOp",EDGE,"E356"),sQuery(id+"F0.wireOp",EDGE,"E357"),sQuery(id+"F0.wireOp",EDGE,"E358"),sQuery(id+"F0.wireOp",EDGE,"E359"),sQuery(id+"F0.wireOp",EDGE,"E360"),sQuery(id+"F0.wireOp",EDGE,"E361"),sQuery(id+"F0.wireOp",EDGE,"E362"),sQuery(id+"F0.wireOp",EDGE,"E363"),sQuery(id+"F0.wireOp",EDGE,"E364"),sQuery(id+"F0.wireOp",EDGE,"E365"),sQuery(id+"F0.wireOp",EDGE,"E366"),sQuery(id+"F0.wireOp",EDGE,"E367"),sQuery(id+"F0.wireOp",EDGE,"E368"),sQuery(id+"F0.wireOp",EDGE,"E369"),sQuery(id+"F0.wireOp",EDGE,"E370"),sQuery(id+"F0.wireOp",EDGE,"E371"),sQuery(id+"F0.wireOp",EDGE,"E372"),sQuery(id+"F0.wireOp",EDGE,"E373"),sQuery(id+"F0.wireOp",EDGE,"E374"),sQuery(id+"F0.wireOp",EDGE,"E375"),sQuery(id+"F0.wireOp",EDGE,"E376"),sQuery(id+"F0.wireOp",EDGE,"E377"),sQuery(id+"F0.wireOp",EDGE,"E378"),sQuery(id+"F0.wireOp",EDGE,"E379"),sQuery(id+"F0.wireOp",EDGE,"E380"),sQuery(id+"F0.wireOp",EDGE,"E381"),sQuery(id+"F0.wireOp",EDGE,"E382"),sQuery(id+"F0.wireOp",EDGE,"E383"),sQuery(id+"F0.wireOp",EDGE,"E384"),sQuery(id+"F0.wireOp",EDGE,"E385"),sQuery(id+"F0.wireOp",EDGE,"E386"),sQuery(id+"F0.wireOp",EDGE,"E387"),sQuery(id+"F0.wireOp",EDGE,"E388"),sQuery(id+"F0.wireOp",EDGE,"E389"),sQuery(id+"F0.wireOp",EDGE,"E390"),sQuery(id+"F0.wireOp",EDGE,"E391"),sQuery(id+"F0.wireOp",EDGE,"E392"),sQuery(id+"F0.wireOp",EDGE,"E393"),sQuery(id+"F0.wireOp",EDGE,"E394"),sQuery(id+"F0.wireOp",EDGE,"E395"),sQuery(id+"F0.wireOp",EDGE,"E396"),sQuery(id+"F0.wireOp",EDGE,"E397"),sQuery(id+"F0.wireOp",EDGE,"E398")])],"isStart":false});
            var sketch = newSketch(context, id + "F3", { "sketchPlane" : qUnion([Q0])});
            skCircle(sketch, "E399", {"center": v(-9.94, 30.51) * mm, "radius": 2.2 * mm});
            skCircle(sketch, "E400", {"center": v(30.06, -9.49) * mm, "radius": 2.2 * mm});
            skSolve(sketch);
        }
        {
            var Q0;
            Q0 = qSketchRegion(id + "F3", true);
            extrude(context, id + "F4", {"entities" : qUnion([Q0]), "operationType" : NewBodyOperationType.REMOVE, "oppositeDirection" : true, "depth" : 25 * mm});
        }
        {
            var Q0;
            Q0=makeQuery(id+"F0.imprint","IMPRINT",FACE,{"disambiguationData":[TD([[makeQuery(id+"F0.imprint","IMPRINT",EDGE,{"derivedFrom":sQuery(id+"F0.wireOp",EDGE,"E0")}),-1.0]])]});
            extrude(context, id + "F5", {"entities" : qUnion([Q0]), "oppositeDirection" : true, "depth" : 2 * mm});
        }
        {
            var Q0;
            Q0=makeQuery(id+"F5.opExtrude","CAP_FACE",FACE,{"disambiguationData":[OSD([sQuery(id+"F0.wireOp",EDGE,"E0"),sQuery(id+"F0.wireOp",EDGE,"E1"),sQuery(id+"F0.wireOp",EDGE,"E2"),sQuery(id+"F0.wireOp",EDGE,"E3"),sQuery(id+"F0.wireOp",EDGE,"E4"),sQuery(id+"F0.wireOp",EDGE,"E5"),sQuery(id+"F0.wireOp",EDGE,"E6"),sQuery(id+"F0.wireOp",EDGE,"E7"),sQuery(id+"F0.wireOp",EDGE,"E8"),sQuery(id+"F0.wireOp",EDGE,"E9"),sQuery(id+"F0.wireOp",EDGE,"E10"),sQuery(id+"F0.wireOp",EDGE,"E11"),sQuery(id+"F0.wireOp",EDGE,"E12"),sQuery(id+"F0.wireOp",EDGE,"E13"),sQuery(id+"F0.wireOp",EDGE,"E14"),sQuery(id+"F0.wireOp",EDGE,"E15"),sQuery(id+"F0.wireOp",EDGE,"E16"),sQuery(id+"F0.wireOp",EDGE,"E17"),sQuery(id+"F0.wireOp",EDGE,"E18"),sQuery(id+"F0.wireOp",EDGE,"E19"),sQuery(id+"F0.wireOp",EDGE,"E20"),sQuery(id+"F0.wireOp",EDGE,"E21"),sQuery(id+"F0.wireOp",EDGE,"E22"),sQuery(id+"F0.wireOp",EDGE,"E23"),sQuery(id+"F0.wireOp",EDGE,"E24"),sQuery(id+"F0.wireOp",EDGE,"E25"),sQuery(id+"F0.wireOp",EDGE,"E26"),sQuery(id+"F0.wireOp",EDGE,"E27"),sQuery(id+"F0.wireOp",EDGE,"E28"),sQuery(id+"F0.wireOp",EDGE,"E29"),sQuery(id+"F0.wireOp",EDGE,"E30"),sQuery(id+"F0.wireOp",EDGE,"E31"),sQuery(id+"F0.wireOp",EDGE,"E32"),sQuery(id+"F0.wireOp",EDGE,"E33"),sQuery(id+"F0.wireOp",EDGE,"E34"),sQuery(id+"F0.wireOp",EDGE,"E35"),sQuery(id+"F0.wireOp",EDGE,"E36"),sQuery(id+"F0.wireOp",EDGE,"E37"),sQuery(id+"F0.wireOp",EDGE,"E38"),sQuery(id+"F0.wireOp",EDGE,"E39"),sQuery(id+"F0.wireOp",EDGE,"E40"),sQuery(id+"F0.wireOp",EDGE,"E41"),sQuery(id+"F0.wireOp",EDGE,"E42"),sQuery(id+"F0.wireOp",EDGE,"E43"),sQuery(id+"F0.wireOp",EDGE,"E44"),sQuery(id+"F0.wireOp",EDGE,"E45"),sQuery(id+"F0.wireOp",EDGE,"E46"),sQuery(id+"F0.wireOp",EDGE,"E47"),sQuery(id+"F0.wireOp",EDGE,"E48"),sQuery(id+"F0.wireOp",EDGE,"E49"),sQuery(id+"F0.wireOp",EDGE,"E50"),sQuery(id+"F0.wireOp",EDGE,"E51"),sQuery(id+"F0.wireOp",EDGE,"E52"),sQuery(id+"F0.wireOp",EDGE,"E53"),sQuery(id+"F0.wireOp",EDGE,"E54"),sQuery(id+"F0.wireOp",EDGE,"E55"),sQuery(id+"F0.wireOp",EDGE,"E56"),sQuery(id+"F0.wireOp",EDGE,"E57"),sQuery(id+"F0.wireOp",EDGE,"E58"),sQuery(id+"F0.wireOp",EDGE,"E59"),sQuery(id+"F0.wireOp",EDGE,"E60"),sQuery(id+"F0.wireOp",EDGE,"E61"),sQuery(id+"F0.wireOp",EDGE,"E62"),sQuery(id+"F0.wireOp",EDGE,"E63"),sQuery(id+"F0.wireOp",EDGE,"E64"),sQuery(id+"F0.wireOp",EDGE,"E65"),sQuery(id+"F0.wireOp",EDGE,"E66"),sQuery(id+"F0.wireOp",EDGE,"E67"),sQuery(id+"F0.wireOp",EDGE,"E68"),sQuery(id+"F0.wireOp",EDGE,"E69"),sQuery(id+"F0.wireOp",EDGE,"E70"),sQuery(id+"F0.wireOp",EDGE,"E71"),sQuery(id+"F0.wireOp",EDGE,"E72"),sQuery(id+"F0.wireOp",EDGE,"E73"),sQuery(id+"F0.wireOp",EDGE,"E74"),sQuery(id+"F0.wireOp",EDGE,"E75"),sQuery(id+"F0.wireOp",EDGE,"E76"),sQuery(id+"F0.wireOp",EDGE,"E77"),sQuery(id+"F0.wireOp",EDGE,"E78"),sQuery(id+"F0.wireOp",EDGE,"E79"),sQuery(id+"F0.wireOp",EDGE,"E80"),sQuery(id+"F0.wireOp",EDGE,"E81"),sQuery(id+"F0.wireOp",EDGE,"E82"),sQuery(id+"F0.wireOp",EDGE,"E83"),sQuery(id+"F0.wireOp",EDGE,"E84"),sQuery(id+"F0.wireOp",EDGE,"E85"),sQuery(id+"F0.wireOp",EDGE,"E86"),sQuery(id+"F0.wireOp",EDGE,"E87"),sQuery(id+"F0.wireOp",EDGE,"E88"),sQuery(id+"F0.wireOp",EDGE,"E89"),sQuery(id+"F0.wireOp",EDGE,"E90"),sQuery(id+"F0.wireOp",EDGE,"E91"),sQuery(id+"F0.wireOp",EDGE,"E92"),sQuery(id+"F0.wireOp",EDGE,"E93"),sQuery(id+"F0.wireOp",EDGE,"E94"),sQuery(id+"F0.wireOp",EDGE,"E95"),sQuery(id+"F0.wireOp",EDGE,"E96"),sQuery(id+"F0.wireOp",EDGE,"E97"),sQuery(id+"F0.wireOp",EDGE,"E98"),sQuery(id+"F0.wireOp",EDGE,"E99"),sQuery(id+"F0.wireOp",EDGE,"E100"),sQuery(id+"F0.wireOp",EDGE,"E101"),sQuery(id+"F0.wireOp",EDGE,"E102"),sQuery(id+"F0.wireOp",EDGE,"E103"),sQuery(id+"F0.wireOp",EDGE,"E104"),sQuery(id+"F0.wireOp",EDGE,"E105"),sQuery(id+"F0.wireOp",EDGE,"E106"),sQuery(id+"F0.wireOp",EDGE,"E107"),sQuery(id+"F0.wireOp",EDGE,"E108"),sQuery(id+"F0.wireOp",EDGE,"E109"),sQuery(id+"F0.wireOp",EDGE,"E110"),sQuery(id+"F0.wireOp",EDGE,"E111"),sQuery(id+"F0.wireOp",EDGE,"E112"),sQuery(id+"F0.wireOp",EDGE,"E113"),sQuery(id+"F0.wireOp",EDGE,"E114"),sQuery(id+"F0.wireOp",EDGE,"E115"),sQuery(id+"F0.wireOp",EDGE,"E116"),sQuery(id+"F0.wireOp",EDGE,"E117"),sQuery(id+"F0.wireOp",EDGE,"E118"),sQuery(id+"F0.wireOp",EDGE,"E119"),sQuery(id+"F0.wireOp",EDGE,"E120"),sQuery(id+"F0.wireOp",EDGE,"E121"),sQuery(id+"F0.wireOp",EDGE,"E122"),sQuery(id+"F0.wireOp",EDGE,"E123"),sQuery(id+"F0.wireOp",EDGE,"E124"),sQuery(id+"F0.wireOp",EDGE,"E125"),sQuery(id+"F0.wireOp",EDGE,"E126"),sQuery(id+"F0.wireOp",EDGE,"E127"),sQuery(id+"F0.wireOp",EDGE,"E128"),sQuery(id+"F0.wireOp",EDGE,"E129"),sQuery(id+"F0.wireOp",EDGE,"E130"),sQuery(id+"F0.wireOp",EDGE,"E131"),sQuery(id+"F0.wireOp",EDGE,"E132"),sQuery(id+"F0.wireOp",EDGE,"E133"),sQuery(id+"F0.wireOp",EDGE,"E143"),sQuery(id+"F0.wireOp",EDGE,"E144"),sQuery(id+"F0.wireOp",EDGE,"E145"),sQuery(id+"F0.wireOp",EDGE,"E146"),sQuery(id+"F0.wireOp",EDGE,"E147"),sQuery(id+"F0.wireOp",EDGE,"E148"),sQuery(id+"F0.wireOp",EDGE,"E149"),sQuery(id+"F0.wireOp",EDGE,"E150"),sQuery(id+"F0.wireOp",EDGE,"E151"),sQuery(id+"F0.wireOp",EDGE,"E152"),sQuery(id+"F0.wireOp",EDGE,"E153"),sQuery(id+"F0.wireOp",EDGE,"E154"),sQuery(id+"F0.wireOp",EDGE,"E155"),sQuery(id+"F0.wireOp",EDGE,"E156"),sQuery(id+"F0.wireOp",EDGE,"E157"),sQuery(id+"F0.wireOp",EDGE,"E158"),sQuery(id+"F0.wireOp",EDGE,"E159"),sQuery(id+"F0.wireOp",EDGE,"E160"),sQuery(id+"F0.wireOp",EDGE,"E161"),sQuery(id+"F0.wireOp",EDGE,"E162"),sQuery(id+"F0.wireOp",EDGE,"E163"),sQuery(id+"F0.wireOp",EDGE,"E164"),sQuery(id+"F0.wireOp",EDGE,"E165"),sQuery(id+"F0.wireOp",EDGE,"E166"),sQuery(id+"F0.wireOp",EDGE,"E167"),sQuery(id+"F0.wireOp",EDGE,"E168"),sQuery(id+"F0.wireOp",EDGE,"E169"),sQuery(id+"F0.wireOp",EDGE,"E170"),sQuery(id+"F0.wireOp",EDGE,"E171"),sQuery(id+"F0.wireOp",EDGE,"E172"),sQuery(id+"F0.wireOp",EDGE,"E173"),sQuery(id+"F0.wireOp",EDGE,"E174"),sQuery(id+"F0.wireOp",EDGE,"E175"),sQuery(id+"F0.wireOp",EDGE,"E176"),sQuery(id+"F0.wireOp",EDGE,"E177"),sQuery(id+"F0.wireOp",EDGE,"E178"),sQuery(id+"F0.wireOp",EDGE,"E179"),sQuery(id+"F0.wireOp",EDGE,"E180"),sQuery(id+"F0.wireOp",EDGE,"E181"),sQuery(id+"F0.wireOp",EDGE,"E182"),sQuery(id+"F0.wireOp",EDGE,"E183"),sQuery(id+"F0.wireOp",EDGE,"E184"),sQuery(id+"F0.wireOp",EDGE,"E185"),sQuery(id+"F0.wireOp",EDGE,"E186"),sQuery(id+"F0.wireOp",EDGE,"E187"),sQuery(id+"F0.wireOp",EDGE,"E188"),sQuery(id+"F0.wireOp",EDGE,"E189"),sQuery(id+"F0.wireOp",EDGE,"E190"),sQuery(id+"F0.wireOp",EDGE,"E191"),sQuery(id+"F0.wireOp",EDGE,"E192"),sQuery(id+"F0.wireOp",EDGE,"E193"),sQuery(id+"F0.wireOp",EDGE,"E194"),sQuery(id+"F0.wireOp",EDGE,"E195"),sQuery(id+"F0.wireOp",EDGE,"E196"),sQuery(id+"F0.wireOp",EDGE,"E197"),sQuery(id+"F0.wireOp",EDGE,"E198"),sQuery(id+"F0.wireOp",EDGE,"E199"),sQuery(id+"F0.wireOp",EDGE,"E200"),sQuery(id+"F0.wireOp",EDGE,"E201"),sQuery(id+"F0.wireOp",EDGE,"E202"),sQuery(id+"F0.wireOp",EDGE,"E203"),sQuery(id+"F0.wireOp",EDGE,"E204"),sQuery(id+"F0.wireOp",EDGE,"E205"),sQuery(id+"F0.wireOp",EDGE,"E206"),sQuery(id+"F0.wireOp",EDGE,"E207"),sQuery(id+"F0.wireOp",EDGE,"E208"),sQuery(id+"F0.wireOp",EDGE,"E209"),sQuery(id+"F0.wireOp",EDGE,"E210"),sQuery(id+"F0.wireOp",EDGE,"E211"),sQuery(id+"F0.wireOp",EDGE,"E212"),sQuery(id+"F0.wireOp",EDGE,"E213"),sQuery(id+"F0.wireOp",EDGE,"E214"),sQuery(id+"F0.wireOp",EDGE,"E215"),sQuery(id+"F0.wireOp",EDGE,"E216"),sQuery(id+"F0.wireOp",EDGE,"E217"),sQuery(id+"F0.wireOp",EDGE,"E218"),sQuery(id+"F0.wireOp",EDGE,"E219"),sQuery(id+"F0.wireOp",EDGE,"E220"),sQuery(id+"F0.wireOp",EDGE,"E221"),sQuery(id+"F0.wireOp",EDGE,"E222"),sQuery(id+"F0.wireOp",EDGE,"E223"),sQuery(id+"F0.wireOp",EDGE,"E224"),sQuery(id+"F0.wireOp",EDGE,"E225"),sQuery(id+"F0.wireOp",EDGE,"E226"),sQuery(id+"F0.wireOp",EDGE,"E227"),sQuery(id+"F0.wireOp",EDGE,"E228"),sQuery(id+"F0.wireOp",EDGE,"E229"),sQuery(id+"F0.wireOp",EDGE,"E230"),sQuery(id+"F0.wireOp",EDGE,"E231"),sQuery(id+"F0.wireOp",EDGE,"E232"),sQuery(id+"F0.wireOp",EDGE,"E233"),sQuery(id+"F0.wireOp",EDGE,"E234"),sQuery(id+"F0.wireOp",EDGE,"E235"),sQuery(id+"F0.wireOp",EDGE,"E236"),sQuery(id+"F0.wireOp",EDGE,"E237"),sQuery(id+"F0.wireOp",EDGE,"E238"),sQuery(id+"F0.wireOp",EDGE,"E239"),sQuery(id+"F0.wireOp",EDGE,"E240"),sQuery(id+"F0.wireOp",EDGE,"E241"),sQuery(id+"F0.wireOp",EDGE,"E242"),sQuery(id+"F0.wireOp",EDGE,"E243"),sQuery(id+"F0.wireOp",EDGE,"E244"),sQuery(id+"F0.wireOp",EDGE,"E245"),sQuery(id+"F0.wireOp",EDGE,"E246"),sQuery(id+"F0.wireOp",EDGE,"E247"),sQuery(id+"F0.wireOp",EDGE,"E248"),sQuery(id+"F0.wireOp",EDGE,"E249"),sQuery(id+"F0.wireOp",EDGE,"E250"),sQuery(id+"F0.wireOp",EDGE,"E251"),sQuery(id+"F0.wireOp",EDGE,"E252"),sQuery(id+"F0.wireOp",EDGE,"E253"),sQuery(id+"F0.wireOp",EDGE,"E254"),sQuery(id+"F0.wireOp",EDGE,"E255"),sQuery(id+"F0.wireOp",EDGE,"E256"),sQuery(id+"F0.wireOp",EDGE,"E257"),sQuery(id+"F0.wireOp",EDGE,"E258"),sQuery(id+"F0.wireOp",EDGE,"E259"),sQuery(id+"F0.wireOp",EDGE,"E260"),sQuery(id+"F0.wireOp",EDGE,"E261"),sQuery(id+"F0.wireOp",EDGE,"E262"),sQuery(id+"F0.wireOp",EDGE,"E263"),sQuery(id+"F0.wireOp",EDGE,"E264"),sQuery(id+"F0.wireOp",EDGE,"E265"),sQuery(id+"F0.wireOp",EDGE,"E266"),sQuery(id+"F0.wireOp",EDGE,"E267"),sQuery(id+"F0.wireOp",EDGE,"E268"),sQuery(id+"F0.wireOp",EDGE,"E269"),sQuery(id+"F0.wireOp",EDGE,"E270"),sQuery(id+"F0.wireOp",EDGE,"E271"),sQuery(id+"F0.wireOp",EDGE,"E272"),sQuery(id+"F0.wireOp",EDGE,"E273"),sQuery(id+"F0.wireOp",EDGE,"E274"),sQuery(id+"F0.wireOp",EDGE,"E275"),sQuery(id+"F0.wireOp",EDGE,"E276"),sQuery(id+"F0.wireOp",EDGE,"E277"),sQuery(id+"F0.wireOp",EDGE,"E278"),sQuery(id+"F0.wireOp",EDGE,"E286"),sQuery(id+"F0.wireOp",EDGE,"E287"),sQuery(id+"F0.wireOp",EDGE,"E288"),sQuery(id+"F0.wireOp",EDGE,"E289"),sQuery(id+"F0.wireOp",EDGE,"E290"),sQuery(id+"F0.wireOp",EDGE,"E291"),sQuery(id+"F0.wireOp",EDGE,"E292"),sQuery(id+"F0.wireOp",EDGE,"E293"),sQuery(id+"F0.wireOp",EDGE,"E294"),sQuery(id+"F0.wireOp",EDGE,"E295"),sQuery(id+"F0.wireOp",EDGE,"E296"),sQuery(id+"F0.wireOp",EDGE,"E297"),sQuery(id+"F0.wireOp",EDGE,"E298"),sQuery(id+"F0.wireOp",EDGE,"E299"),sQuery(id+"F0.wireOp",EDGE,"E300"),sQuery(id+"F0.wireOp",EDGE,"E301"),sQuery(id+"F0.wireOp",EDGE,"E302"),sQuery(id+"F0.wireOp",EDGE,"E303"),sQuery(id+"F0.wireOp",EDGE,"E304"),sQuery(id+"F0.wireOp",EDGE,"E305"),sQuery(id+"F0.wireOp",EDGE,"E306"),sQuery(id+"F0.wireOp",EDGE,"E307"),sQuery(id+"F0.wireOp",EDGE,"E308"),sQuery(id+"F0.wireOp",EDGE,"E309"),sQuery(id+"F0.wireOp",EDGE,"E310"),sQuery(id+"F0.wireOp",EDGE,"E311"),sQuery(id+"F0.wireOp",EDGE,"E312"),sQuery(id+"F0.wireOp",EDGE,"E313"),sQuery(id+"F0.wireOp",EDGE,"E314"),sQuery(id+"F0.wireOp",EDGE,"E315"),sQuery(id+"F0.wireOp",EDGE,"E316"),sQuery(id+"F0.wireOp",EDGE,"E317"),sQuery(id+"F0.wireOp",EDGE,"E318"),sQuery(id+"F0.wireOp",EDGE,"E319"),sQuery(id+"F0.wireOp",EDGE,"E320"),sQuery(id+"F0.wireOp",EDGE,"E321"),sQuery(id+"F0.wireOp",EDGE,"E322"),sQuery(id+"F0.wireOp",EDGE,"E323"),sQuery(id+"F0.wireOp",EDGE,"E324"),sQuery(id+"F0.wireOp",EDGE,"E325"),sQuery(id+"F0.wireOp",EDGE,"E326"),sQuery(id+"F0.wireOp",EDGE,"E327"),sQuery(id+"F0.wireOp",EDGE,"E328"),sQuery(id+"F0.wireOp",EDGE,"E329"),sQuery(id+"F0.wireOp",EDGE,"E339"),sQuery(id+"F0.wireOp",EDGE,"E340"),sQuery(id+"F0.wireOp",EDGE,"E341"),sQuery(id+"F0.wireOp",EDGE,"E342"),sQuery(id+"F0.wireOp",EDGE,"E343"),sQuery(id+"F0.wireOp",EDGE,"E344"),sQuery(id+"F0.wireOp",EDGE,"E345"),sQuery(id+"F0.wireOp",EDGE,"E346"),sQuery(id+"F0.wireOp",EDGE,"E347"),sQuery(id+"F0.wireOp",EDGE,"E348"),sQuery(id+"F0.wireOp",EDGE,"E349"),sQuery(id+"F0.wireOp",EDGE,"E350"),sQuery(id+"F0.wireOp",EDGE,"E351"),sQuery(id+"F0.wireOp",EDGE,"E352"),sQuery(id+"F0.wireOp",EDGE,"E353"),sQuery(id+"F0.wireOp",EDGE,"E354"),sQuery(id+"F0.wireOp",EDGE,"E355"),sQuery(id+"F0.wireOp",EDGE,"E356"),sQuery(id+"F0.wireOp",EDGE,"E357"),sQuery(id+"F0.wireOp",EDGE,"E358"),sQuery(id+"F0.wireOp",EDGE,"E359"),sQuery(id+"F0.wireOp",EDGE,"E360"),sQuery(id+"F0.wireOp",EDGE,"E361"),sQuery(id+"F0.wireOp",EDGE,"E362"),sQuery(id+"F0.wireOp",EDGE,"E363"),sQuery(id+"F0.wireOp",EDGE,"E364"),sQuery(id+"F0.wireOp",EDGE,"E365"),sQuery(id+"F0.wireOp",EDGE,"E366"),sQuery(id+"F0.wireOp",EDGE,"E367"),sQuery(id+"F0.wireOp",EDGE,"E368"),sQuery(id+"F0.wireOp",EDGE,"E369"),sQuery(id+"F0.wireOp",EDGE,"E370"),sQuery(id+"F0.wireOp",EDGE,"E371"),sQuery(id+"F0.wireOp",EDGE,"E372"),sQuery(id+"F0.wireOp",EDGE,"E373"),sQuery(id+"F0.wireOp",EDGE,"E374"),sQuery(id+"F0.wireOp",EDGE,"E375"),sQuery(id+"F0.wireOp",EDGE,"E376"),sQuery(id+"F0.wireOp",EDGE,"E377"),sQuery(id+"F0.wireOp",EDGE,"E378"),sQuery(id+"F0.wireOp",EDGE,"E379"),sQuery(id+"F0.wireOp",EDGE,"E380"),sQuery(id+"F0.wireOp",EDGE,"E381"),sQuery(id+"F0.wireOp",EDGE,"E382"),sQuery(id+"F0.wireOp",EDGE,"E383"),sQuery(id+"F0.wireOp",EDGE,"E384"),sQuery(id+"F0.wireOp",EDGE,"E385"),sQuery(id+"F0.wireOp",EDGE,"E386"),sQuery(id+"F0.wireOp",EDGE,"E387"),sQuery(id+"F0.wireOp",EDGE,"E388"),sQuery(id+"F0.wireOp",EDGE,"E389"),sQuery(id+"F0.wireOp",EDGE,"E390"),sQuery(id+"F0.wireOp",EDGE,"E391"),sQuery(id+"F0.wireOp",EDGE,"E392"),sQuery(id+"F0.wireOp",EDGE,"E393"),sQuery(id+"F0.wireOp",EDGE,"E394"),sQuery(id+"F0.wireOp",EDGE,"E395"),sQuery(id+"F0.wireOp",EDGE,"E396"),sQuery(id+"F0.wireOp",EDGE,"E397"),sQuery(id+"F0.wireOp",EDGE,"E398")])],"isStart":true});
            var sketch = newSketch(context, id + "F6", { "sketchPlane" : qUnion([Q0])});
            skCircle(sketch, "E401", {"center": v(-24.14, 36.5) * mm, "radius": 1.82 * mm});
            skCircle(sketch, "E402.1.0.0", {"center": v(-17.83, 36.5) * mm, "radius": 1.82 * mm});
            skCircle(sketch, "E402.2.0.0", {"center": v(-11.52, 36.5) * mm, "radius": 1.82 * mm});
            skCircle(sketch, "E402.3.0.0", {"center": v(-5.21, 36.5) * mm, "radius": 1.82 * mm});
            skCircle(sketch, "E402.4.0.0", {"center": v(1.1, 36.5) * mm, "radius": 1.82 * mm});
            skCircle(sketch, "E402.5.0.0", {"center": v(7.4, 36.5) * mm, "radius": 1.82 * mm});
            skCircle(sketch, "E402.6.0.0", {"center": v(13.71, 36.5) * mm, "radius": 1.82 * mm});
            skCircle(sketch, "E402.7.0.0", {"center": v(20.02, 36.5) * mm, "radius": 1.82 * mm});
            skCircle(sketch, "E402.8.0.0", {"center": v(26.33, 36.5) * mm, "radius": 1.82 * mm});
            skCircle(sketch, "E402.9.0.0", {"center": v(32.64, 36.5) * mm, "radius": 1.82 * mm});
            skLineSegment(sketch, "E402.direction1", {"start": v(-24.14, 36.5) * mm, "end": v(-17.83, 36.5) * mm, "construction": true});
            skCircle(sketch, "E403.1.0.0", {"center": v(32.63, 30.1) * mm, "radius": 1.82 * mm});
            skCircle(sketch, "E403.2.0.0", {"center": v(32.63, 23.7) * mm, "radius": 1.82 * mm});
            skCircle(sketch, "E403.3.0.0", {"center": v(32.62, 17.29) * mm, "radius": 1.82 * mm});
            skCircle(sketch, "E403.4.0.0", {"center": v(32.62, 10.88) * mm, "radius": 1.82 * mm});
            skCircle(sketch, "E403.5.0.0", {"center": v(32.61, 4.48) * mm, "radius": 1.82 * mm});
            skCircle(sketch, "E403.6.0.0", {"center": v(32.6, -1.93) * mm, "radius": 1.82 * mm});
            skCircle(sketch, "E403.7.0.0", {"center": v(32.6, -8.33) * mm, "radius": 1.82 * mm});
            skCircle(sketch, "E403.8.0.0", {"center": v(32.6, -14.74) * mm, "radius": 1.82 * mm});
            skCircle(sketch, "E403.9.0.0", {"center": v(32.6, -21.15) * mm, "radius": 1.82 * mm});
            skLineSegment(sketch, "E403.direction1", {"start": v(32.64, 36.5) * mm, "end": v(32.63, 30.1) * mm, "construction": true});
            skCircle(sketch, "E404.1.0.0", {"center": v(26.31, 30.02) * mm, "radius": 1.82 * mm});
            skCircle(sketch, "E404.2.0.0", {"center": v(26.3, 23.53) * mm, "radius": 1.82 * mm});
            skCircle(sketch, "E404.3.0.0", {"center": v(26.27, 17.04) * mm, "radius": 1.82 * mm});
            skCircle(sketch, "E404.4.0.0", {"center": v(26.25, 10.55) * mm, "radius": 1.82 * mm});
            skCircle(sketch, "E404.5.0.0", {"center": v(26.23, 4.06) * mm, "radius": 1.82 * mm});
            skCircle(sketch, "E404.6.0.0", {"center": v(26.2, -2.42) * mm, "radius": 1.82 * mm});
            skCircle(sketch, "E404.7.0.0", {"center": v(26.19, -8.91) * mm, "radius": 1.82 * mm});
            skCircle(sketch, "E404.8.0.0", {"center": v(26.17, -15.4) * mm, "radius": 1.82 * mm});
            skLineSegment(sketch, "E404.direction1", {"start": v(26.33, 36.5) * mm, "end": v(26.31, 30.02) * mm, "construction": true});
            skSolve(sketch);
        }
        {
            var Q0;
            Q0 = qSketchRegion(id + "F6", true);
            extrude(context, id + "F7", {"entities" : qUnion([Q0]), "operationType" : NewBodyOperationType.REMOVE, "oppositeDirection" : true, "depth" : 5 * mm});
        }
    });
